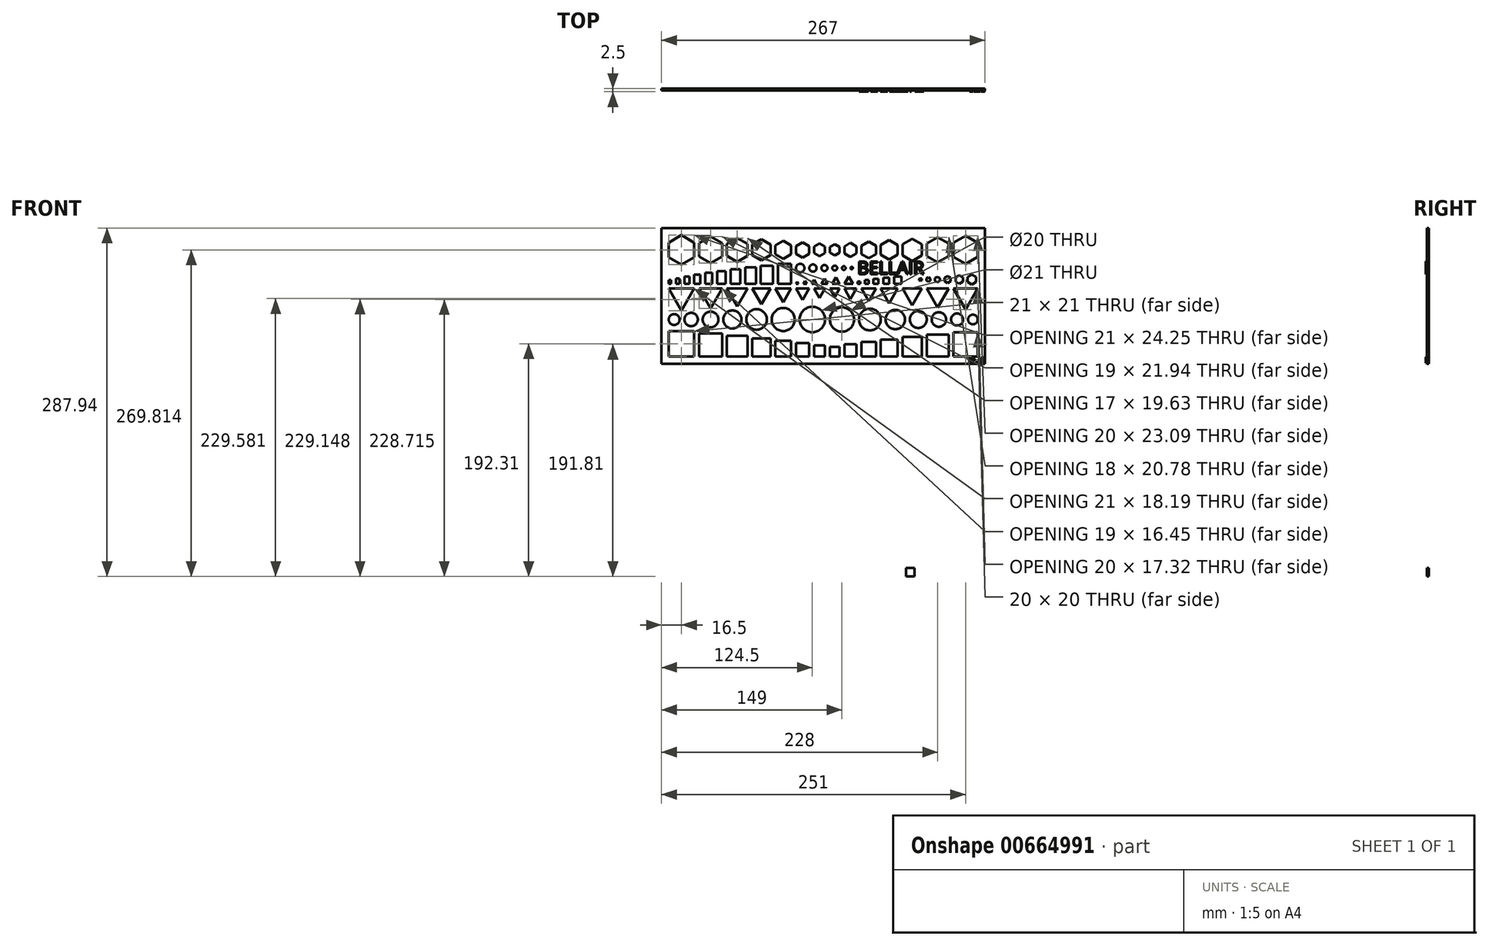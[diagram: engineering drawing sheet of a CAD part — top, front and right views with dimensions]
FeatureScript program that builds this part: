
annotation { "Feature Type Name" : "Feature", "Feature Type Description" : "" }
export const myFeature = defineFeature(function(context is Context, id is Id, definition is map)
    precondition{}
    {
        {
            var Q0;
            Q0=qCreatedBy(makeId("Front.planeOp"),FACE);
            var sketch = newSketch(context, id + "F0", { "sketchPlane" : qUnion([Q0])});
            skLineSegment(sketch, "E0.bottom", {"start": v(0, 0) * mm, "end": v(8, 0) * mm});
            skLineSegment(sketch, "E0.top", {"start": v(0, 8) * mm, "end": v(8, 8) * mm});
            skLineSegment(sketch, "E0.left", {"start": v(0, 0) * mm, "end": v(0, 8) * mm});
            skLineSegment(sketch, "E0.right", {"start": v(8, 0) * mm, "end": v(8, 8) * mm});
            skLineSegment(sketch, "E1.bottom", {"start": v(12, 0) * mm, "end": v(22, 0) * mm});
            skLineSegment(sketch, "E1.top", {"start": v(12, 10) * mm, "end": v(22, 10) * mm});
            skLineSegment(sketch, "E1.left", {"start": v(12, 0) * mm, "end": v(12, 10) * mm});
            skLineSegment(sketch, "E1.right", {"start": v(22, 0) * mm, "end": v(22, 10) * mm});
            skLineSegment(sketch, "E2.bottom", {"start": v(26, 0) * mm, "end": v(38, 0) * mm});
            skLineSegment(sketch, "E2.top", {"start": v(26, 12) * mm, "end": v(38, 12) * mm});
            skLineSegment(sketch, "E2.left", {"start": v(26, 0) * mm, "end": v(26, 12) * mm});
            skLineSegment(sketch, "E2.right", {"start": v(38, 0) * mm, "end": v(38, 12) * mm});
            skLineSegment(sketch, "E3.bottom", {"start": v(42, 0) * mm, "end": v(56, 0) * mm});
            skLineSegment(sketch, "E3.top", {"start": v(42, 14) * mm, "end": v(56, 14) * mm});
            skLineSegment(sketch, "E3.left", {"start": v(42, 0) * mm, "end": v(42, 14) * mm});
            skLineSegment(sketch, "E3.right", {"start": v(56, 0) * mm, "end": v(56, 14) * mm});
            skLineSegment(sketch, "E4.bottom", {"start": v(60, 0) * mm, "end": v(76, 0) * mm});
            skLineSegment(sketch, "E4.top", {"start": v(60, 16) * mm, "end": v(76, 16) * mm});
            skLineSegment(sketch, "E4.left", {"start": v(60, 0) * mm, "end": v(60, 16) * mm});
            skLineSegment(sketch, "E4.right", {"start": v(76, 0) * mm, "end": v(76, 16) * mm});
            skLineSegment(sketch, "E5.bottom", {"start": v(80, 0) * mm, "end": v(98, 0) * mm});
            skLineSegment(sketch, "E5.top", {"start": v(80, 18) * mm, "end": v(98, 18) * mm});
            skLineSegment(sketch, "E5.left", {"start": v(80, 0) * mm, "end": v(80, 18) * mm});
            skLineSegment(sketch, "E5.right", {"start": v(98, 0) * mm, "end": v(98, 18) * mm});
            skLineSegment(sketch, "E6.bottom", {"start": v(102, 0) * mm, "end": v(122, 0) * mm});
            skLineSegment(sketch, "E6.top", {"start": v(102, 20) * mm, "end": v(122, 20) * mm});
            skLineSegment(sketch, "E6.left", {"start": v(102, 0) * mm, "end": v(102, 20) * mm});
            skLineSegment(sketch, "E6.right", {"start": v(122, 0) * mm, "end": v(122, 20) * mm});
            skCircle(sketch, "E7", {"center": v(118, 30.5) * mm, "radius": 4 * mm});
            skCircle(sketch, "E8", {"center": v(105, 30.5) * mm, "radius": 5 * mm});
            skCircle(sketch, "E9", {"center": v(73, 30.5) * mm, "radius": 7 * mm});
            skCircle(sketch, "E10", {"center": v(90, 30.5) * mm, "radius": 6 * mm});
            skCircle(sketch, "E11", {"center": v(54, 30.5) * mm, "radius": 8 * mm});
            skCircle(sketch, "E12", {"center": v(33, 30.5) * mm, "radius": 9 * mm});
            skCircle(sketch, "E13", {"center": v(10, 30.5) * mm, "radius": 10 * mm});
            skLineSegment(sketch, "E14.bottom", {"start": v(-4, 0) * mm, "end": v(-13, 0) * mm});
            skLineSegment(sketch, "E14.top", {"start": v(-4, 9) * mm, "end": v(-13, 9) * mm});
            skLineSegment(sketch, "E14.left", {"start": v(-4, 0) * mm, "end": v(-4, 9) * mm});
            skLineSegment(sketch, "E14.right", {"start": v(-13, 0) * mm, "end": v(-13, 9) * mm});
            skLineSegment(sketch, "E15.bottom", {"start": v(-17, 0) * mm, "end": v(-28, 0) * mm});
            skLineSegment(sketch, "E15.top", {"start": v(-17, 11) * mm, "end": v(-28, 11) * mm});
            skLineSegment(sketch, "E15.left", {"start": v(-17, 0) * mm, "end": v(-17, 11) * mm});
            skLineSegment(sketch, "E15.right", {"start": v(-28, 0) * mm, "end": v(-28, 11) * mm});
            skLineSegment(sketch, "E16.bottom", {"start": v(-32, 0) * mm, "end": v(-45, 0) * mm});
            skLineSegment(sketch, "E16.top", {"start": v(-32, 13) * mm, "end": v(-45, 13) * mm});
            skLineSegment(sketch, "E16.left", {"start": v(-32, 0) * mm, "end": v(-32, 13) * mm});
            skLineSegment(sketch, "E16.right", {"start": v(-45, 0) * mm, "end": v(-45, 13) * mm});
            skLineSegment(sketch, "E17.bottom", {"start": v(-49, 0) * mm, "end": v(-64, 0) * mm});
            skLineSegment(sketch, "E17.top", {"start": v(-49, 15) * mm, "end": v(-64, 15) * mm});
            skLineSegment(sketch, "E17.left", {"start": v(-49, 0) * mm, "end": v(-49, 15) * mm});
            skLineSegment(sketch, "E17.right", {"start": v(-64, 0) * mm, "end": v(-64, 15) * mm});
            skLineSegment(sketch, "E18.bottom", {"start": v(-68, 0) * mm, "end": v(-85, 0) * mm});
            skLineSegment(sketch, "E18.top", {"start": v(-68, 17) * mm, "end": v(-85, 17) * mm});
            skLineSegment(sketch, "E18.left", {"start": v(-68, 0) * mm, "end": v(-68, 17) * mm});
            skLineSegment(sketch, "E18.right", {"start": v(-85, 0) * mm, "end": v(-85, 17) * mm});
            skLineSegment(sketch, "E19.bottom", {"start": v(-89, 0) * mm, "end": v(-108, 0) * mm});
            skLineSegment(sketch, "E19.top", {"start": v(-89, 19) * mm, "end": v(-108, 19) * mm});
            skLineSegment(sketch, "E19.left", {"start": v(-89, 0) * mm, "end": v(-89, 19) * mm});
            skLineSegment(sketch, "E19.right", {"start": v(-108, 0) * mm, "end": v(-108, 19) * mm});
            skLineSegment(sketch, "E20.bottom", {"start": v(-112, 0) * mm, "end": v(-133, 0) * mm});
            skLineSegment(sketch, "E20.top", {"start": v(-112, 21) * mm, "end": v(-133, 21) * mm});
            skLineSegment(sketch, "E20.left", {"start": v(-112, 0) * mm, "end": v(-112, 21) * mm});
            skLineSegment(sketch, "E20.right", {"start": v(-133, 0) * mm, "end": v(-133, 21) * mm});
            skCircle(sketch, "E21", {"center": v(-38.5, 30.5) * mm, "radius": 9.5 * mm});
            skCircle(sketch, "E22", {"center": v(-60.5, 30.5) * mm, "radius": 8.5 * mm});
            skCircle(sketch, "E23", {"center": v(-80.5, 30.5) * mm, "radius": 7.5 * mm});
            skCircle(sketch, "E24", {"center": v(-128.5, 30.5) * mm, "radius": 4.5 * mm});
            skCircle(sketch, "E25", {"center": v(-98.5, 30.5) * mm, "radius": 6.5 * mm});
            skCircle(sketch, "E26", {"center": v(-114.5, 30.5) * mm, "radius": 5.5 * mm});
            skCircle(sketch, "E27", {"center": v(-14.5, 30.5) * mm, "radius": 10.5 * mm});
            skCircle(sketch, "E28.cCircle", {"center": v(4, 53.69) * mm, "radius": 2.3 * mm, "construction": true});
            skLineSegment(sketch, "E28.0", {"start": v(0, 56) * mm, "end": v(8, 56) * mm});
            skLineSegment(sketch, "E28.1", {"start": v(8, 56) * mm, "end": v(4, 49.07) * mm});
            skLineSegment(sketch, "E28.2", {"start": v(4, 49.07) * mm, "end": v(0, 56) * mm});
            skPoint(sketch, "E28.0.midPoint", {"position": v(4, 56) * mm});
            skCircle(sketch, "E29.cCircle", {"center": v(17, 53.11) * mm, "radius": 2.89 * mm, "construction": true});
            skLineSegment(sketch, "E29.0", {"start": v(12, 56) * mm, "end": v(22, 56) * mm});
            skLineSegment(sketch, "E29.1", {"start": v(22, 56) * mm, "end": v(17, 47.34) * mm});
            skLineSegment(sketch, "E29.2", {"start": v(17, 47.34) * mm, "end": v(12, 56) * mm});
            skPoint(sketch, "E29.0.midPoint", {"position": v(17, 56) * mm});
            skCircle(sketch, "E30.cCircle", {"center": v(32, 52.53) * mm, "radius": 3.46 * mm, "construction": true});
            skLineSegment(sketch, "E30.0", {"start": v(26, 56) * mm, "end": v(38, 56) * mm});
            skLineSegment(sketch, "E30.1", {"start": v(38, 56) * mm, "end": v(32, 45.6) * mm});
            skLineSegment(sketch, "E30.2", {"start": v(32, 45.6) * mm, "end": v(26, 56) * mm});
            skPoint(sketch, "E30.0.midPoint", {"position": v(32, 56) * mm});
            skCircle(sketch, "E31.cCircle", {"center": v(49, 51.96) * mm, "radius": 4.04 * mm, "construction": true});
            skLineSegment(sketch, "E31.0", {"start": v(42, 56) * mm, "end": v(56, 56) * mm});
            skLineSegment(sketch, "E31.1", {"start": v(56, 56) * mm, "end": v(49, 43.87) * mm});
            skLineSegment(sketch, "E31.2", {"start": v(49, 43.87) * mm, "end": v(42, 56) * mm});
            skPoint(sketch, "E31.0.midPoint", {"position": v(49, 56) * mm});
            skCircle(sketch, "E32.cCircle", {"center": v(68, 51.38) * mm, "radius": 4.62 * mm, "construction": true});
            skLineSegment(sketch, "E32.0", {"start": v(60, 56) * mm, "end": v(76, 56) * mm});
            skLineSegment(sketch, "E32.1", {"start": v(76, 56) * mm, "end": v(68, 42.14) * mm});
            skLineSegment(sketch, "E32.2", {"start": v(68, 42.14) * mm, "end": v(60, 56) * mm});
            skPoint(sketch, "E32.0.midPoint", {"position": v(68, 56) * mm});
            skCircle(sketch, "E33.cCircle", {"center": v(89, 50.8) * mm, "radius": 5.2 * mm, "construction": true});
            skLineSegment(sketch, "E33.0", {"start": v(80, 56) * mm, "end": v(98, 56) * mm});
            skLineSegment(sketch, "E33.1", {"start": v(98, 56) * mm, "end": v(89, 40.4) * mm});
            skLineSegment(sketch, "E33.2", {"start": v(89, 40.4) * mm, "end": v(80, 56) * mm});
            skPoint(sketch, "E33.0.midPoint", {"position": v(89, 56) * mm});
            skCircle(sketch, "E34.cCircle", {"center": v(112, 50.22) * mm, "radius": 5.77 * mm, "construction": true});
            skLineSegment(sketch, "E34.0", {"start": v(102, 56) * mm, "end": v(122, 56) * mm});
            skLineSegment(sketch, "E34.1", {"start": v(122, 56) * mm, "end": v(112, 38.68) * mm});
            skLineSegment(sketch, "E34.2", {"start": v(112, 38.68) * mm, "end": v(102, 56) * mm});
            skPoint(sketch, "E34.0.midPoint", {"position": v(112, 56) * mm});
            skCircle(sketch, "E35.cCircle", {"center": v(-8.5, 53.4) * mm, "radius": 2.6 * mm, "construction": true});
            skLineSegment(sketch, "E35.0", {"start": v(-13, 56) * mm, "end": v(-4, 56) * mm});
            skLineSegment(sketch, "E35.1", {"start": v(-4, 56) * mm, "end": v(-8.5, 48.2) * mm});
            skLineSegment(sketch, "E35.2", {"start": v(-8.5, 48.2) * mm, "end": v(-13, 56) * mm});
            skPoint(sketch, "E35.0.midPoint", {"position": v(-8.5, 56) * mm});
            skCircle(sketch, "E36.cCircle", {"center": v(-22.5, 52.82) * mm, "radius": 3.18 * mm, "construction": true});
            skLineSegment(sketch, "E36.0", {"start": v(-28, 56) * mm, "end": v(-17, 56) * mm});
            skLineSegment(sketch, "E36.1", {"start": v(-17, 56) * mm, "end": v(-22.5, 46.47) * mm});
            skLineSegment(sketch, "E36.2", {"start": v(-22.5, 46.47) * mm, "end": v(-28, 56) * mm});
            skPoint(sketch, "E36.0.midPoint", {"position": v(-22.5, 56) * mm});
            skCircle(sketch, "E37.cCircle", {"center": v(-38.5, 52.25) * mm, "radius": 3.75 * mm, "construction": true});
            skLineSegment(sketch, "E37.0", {"start": v(-45, 56) * mm, "end": v(-32, 56) * mm});
            skLineSegment(sketch, "E37.1", {"start": v(-32, 56) * mm, "end": v(-38.5, 44.74) * mm});
            skLineSegment(sketch, "E37.2", {"start": v(-38.5, 44.74) * mm, "end": v(-45, 56) * mm});
            skPoint(sketch, "E37.0.midPoint", {"position": v(-38.5, 56) * mm});
            skCircle(sketch, "E38.cCircle", {"center": v(-56.5, 51.67) * mm, "radius": 4.33 * mm, "construction": true});
            skLineSegment(sketch, "E38.0", {"start": v(-64, 56) * mm, "end": v(-49, 56) * mm});
            skLineSegment(sketch, "E38.1", {"start": v(-49, 56) * mm, "end": v(-56.5, 43) * mm});
            skLineSegment(sketch, "E38.2", {"start": v(-56.5, 43) * mm, "end": v(-64, 56) * mm});
            skPoint(sketch, "E38.0.midPoint", {"position": v(-56.5, 56) * mm});
            skCircle(sketch, "E39.cCircle", {"center": v(-76.5, 51.1) * mm, "radius": 4.9 * mm, "construction": true});
            skLineSegment(sketch, "E39.0", {"start": v(-85, 56) * mm, "end": v(-68, 56) * mm});
            skLineSegment(sketch, "E39.1", {"start": v(-68, 56) * mm, "end": v(-76.5, 41.28) * mm});
            skLineSegment(sketch, "E39.2", {"start": v(-76.5, 41.28) * mm, "end": v(-85, 56) * mm});
            skPoint(sketch, "E39.0.midPoint", {"position": v(-76.5, 56) * mm});
            skCircle(sketch, "E40.cCircle", {"center": v(-98.5, 50.51) * mm, "radius": 5.48 * mm, "construction": true});
            skLineSegment(sketch, "E40.0", {"start": v(-108, 56) * mm, "end": v(-89, 56) * mm});
            skLineSegment(sketch, "E40.1", {"start": v(-89, 56) * mm, "end": v(-98.5, 39.54) * mm});
            skLineSegment(sketch, "E40.2", {"start": v(-98.5, 39.54) * mm, "end": v(-108, 56) * mm});
            skPoint(sketch, "E40.0.midPoint", {"position": v(-98.5, 56) * mm});
            skCircle(sketch, "E41.cCircle", {"center": v(-122.5, 49.94) * mm, "radius": 6.06 * mm, "construction": true});
            skLineSegment(sketch, "E41.0", {"start": v(-133, 56) * mm, "end": v(-112, 56) * mm});
            skLineSegment(sketch, "E41.1", {"start": v(-112, 56) * mm, "end": v(-122.5, 37.81) * mm});
            skLineSegment(sketch, "E41.2", {"start": v(-122.5, 37.81) * mm, "end": v(-133, 56) * mm});
            skPoint(sketch, "E41.0.midPoint", {"position": v(-122.5, 56) * mm});
            skLineSegment(sketch, "E42.bottom", {"start": v(-133, 60) * mm, "end": v(-131, 60) * mm});
            skLineSegment(sketch, "E42.top", {"start": v(-133, 63) * mm, "end": v(-131, 63) * mm});
            skLineSegment(sketch, "E42.left", {"start": v(-133, 60) * mm, "end": v(-133, 63) * mm});
            skLineSegment(sketch, "E42.right", {"start": v(-131, 60) * mm, "end": v(-131, 63) * mm});
            skLineSegment(sketch, "E43.bottom", {"start": v(-127, 60) * mm, "end": v(-124, 60) * mm});
            skLineSegment(sketch, "E43.top", {"start": v(-127, 64.5) * mm, "end": v(-124, 64.5) * mm});
            skLineSegment(sketch, "E43.left", {"start": v(-127, 60) * mm, "end": v(-127, 64.5) * mm});
            skLineSegment(sketch, "E43.right", {"start": v(-124, 60) * mm, "end": v(-124, 64.5) * mm});
            skLineSegment(sketch, "E44.bottom", {"start": v(-120, 60) * mm, "end": v(-116, 60) * mm});
            skLineSegment(sketch, "E44.top", {"start": v(-120, 66) * mm, "end": v(-116, 66) * mm});
            skLineSegment(sketch, "E44.left", {"start": v(-120, 60) * mm, "end": v(-120, 66) * mm});
            skLineSegment(sketch, "E44.right", {"start": v(-116, 60) * mm, "end": v(-116, 66) * mm});
            skLineSegment(sketch, "E45.bottom", {"start": v(-112, 60) * mm, "end": v(-107, 60) * mm});
            skLineSegment(sketch, "E45.top", {"start": v(-112, 67.5) * mm, "end": v(-107, 67.5) * mm});
            skLineSegment(sketch, "E45.left", {"start": v(-112, 60) * mm, "end": v(-112, 67.5) * mm});
            skLineSegment(sketch, "E45.right", {"start": v(-107, 60) * mm, "end": v(-107, 67.5) * mm});
            skLineSegment(sketch, "E46.bottom", {"start": v(-103, 60) * mm, "end": v(-97, 60) * mm});
            skLineSegment(sketch, "E46.top", {"start": v(-103, 69) * mm, "end": v(-97, 69) * mm});
            skLineSegment(sketch, "E46.left", {"start": v(-103, 60) * mm, "end": v(-103, 69) * mm});
            skLineSegment(sketch, "E46.right", {"start": v(-97, 60) * mm, "end": v(-97, 69) * mm});
            skLineSegment(sketch, "E47.bottom", {"start": v(-93, 60) * mm, "end": v(-86, 60) * mm});
            skLineSegment(sketch, "E47.top", {"start": v(-93, 70.5) * mm, "end": v(-86, 70.5) * mm});
            skLineSegment(sketch, "E47.left", {"start": v(-93, 60) * mm, "end": v(-93, 70.5) * mm});
            skLineSegment(sketch, "E47.right", {"start": v(-86, 60) * mm, "end": v(-86, 70.5) * mm});
            skLineSegment(sketch, "E48.bottom", {"start": v(-82, 60) * mm, "end": v(-74, 60) * mm});
            skLineSegment(sketch, "E48.top", {"start": v(-82, 72) * mm, "end": v(-74, 72) * mm});
            skLineSegment(sketch, "E48.left", {"start": v(-82, 60) * mm, "end": v(-82, 72) * mm});
            skLineSegment(sketch, "E48.right", {"start": v(-74, 60) * mm, "end": v(-74, 72) * mm});
            skLineSegment(sketch, "E49.bottom", {"start": v(-70, 60) * mm, "end": v(-61, 60) * mm});
            skLineSegment(sketch, "E49.top", {"start": v(-70, 73.5) * mm, "end": v(-61, 73.5) * mm});
            skLineSegment(sketch, "E49.left", {"start": v(-70, 60) * mm, "end": v(-70, 73.5) * mm});
            skLineSegment(sketch, "E49.right", {"start": v(-61, 60) * mm, "end": v(-61, 73.5) * mm});
            skLineSegment(sketch, "E50.bottom", {"start": v(-57, 60) * mm, "end": v(-47, 60) * mm});
            skLineSegment(sketch, "E50.top", {"start": v(-57, 75) * mm, "end": v(-47, 75) * mm});
            skLineSegment(sketch, "E50.left", {"start": v(-57, 60) * mm, "end": v(-57, 75) * mm});
            skLineSegment(sketch, "E50.right", {"start": v(-47, 60) * mm, "end": v(-47, 75) * mm});
            skLineSegment(sketch, "E51.bottom", {"start": v(-43, 60) * mm, "end": v(-32, 60) * mm});
            skLineSegment(sketch, "E51.top", {"start": v(-43, 76.5) * mm, "end": v(-32, 76.5) * mm});
            skLineSegment(sketch, "E51.left", {"start": v(-43, 60) * mm, "end": v(-43, 76.5) * mm});
            skLineSegment(sketch, "E51.right", {"start": v(-32, 60) * mm, "end": v(-32, 76.5) * mm});
            skCircle(sketch, "E52.cCircle", {"center": v(-27, 60.58) * mm, "radius": 0.58 * mm, "construction": true});
            skLineSegment(sketch, "E52.0", {"start": v(-26, 60) * mm, "end": v(-28, 60) * mm});
            skLineSegment(sketch, "E52.1", {"start": v(-28, 60) * mm, "end": v(-27, 61.73) * mm});
            skLineSegment(sketch, "E52.2", {"start": v(-27, 61.73) * mm, "end": v(-26, 60) * mm});
            skPoint(sketch, "E52.0.midPoint", {"position": v(-27, 60) * mm});
            skCircle(sketch, "E53.cCircle", {"center": v(-20.5, 60.86) * mm, "radius": 0.87 * mm, "construction": true});
            skPoint(sketch, "E53.cCircle.perimeterSnap0", {"position": v(-5.5, 60) * mm});
            skLineSegment(sketch, "E53.0", {"start": v(-19, 60) * mm, "end": v(-22, 60) * mm});
            skLineSegment(sketch, "E53.1", {"start": v(-22, 60) * mm, "end": v(-20.5, 62.6) * mm});
            skLineSegment(sketch, "E53.2", {"start": v(-20.5, 62.6) * mm, "end": v(-19, 60) * mm});
            skPoint(sketch, "E53.0.midPoint", {"position": v(-20.5, 60) * mm});
            skPoint(sketch, "E53.0.midPoint.positionSnap0", {"position": v(-5.5, 60) * mm});
            skCircle(sketch, "E54.cCircle", {"center": v(-13, 61.15) * mm, "radius": 1.15 * mm, "construction": true});
            skLineSegment(sketch, "E54.0", {"start": v(-11, 60) * mm, "end": v(-15, 60) * mm});
            skLineSegment(sketch, "E54.1", {"start": v(-15, 60) * mm, "end": v(-13, 63.46) * mm});
            skLineSegment(sketch, "E54.2", {"start": v(-13, 63.46) * mm, "end": v(-11, 60) * mm});
            skPoint(sketch, "E54.0.midPoint", {"position": v(-13, 60) * mm});
            skCircle(sketch, "E55.cCircle", {"center": v(-4.5, 61.44) * mm, "radius": 1.44 * mm, "construction": true});
            skLineSegment(sketch, "E55.0", {"start": v(-2, 60) * mm, "end": v(-7, 60) * mm});
            skLineSegment(sketch, "E55.1", {"start": v(-7, 60) * mm, "end": v(-4.5, 64.33) * mm});
            skLineSegment(sketch, "E55.2", {"start": v(-4.5, 64.33) * mm, "end": v(-2, 60) * mm});
            skPoint(sketch, "E55.0.midPoint", {"position": v(-4.5, 60) * mm});
            skCircle(sketch, "E56.cCircle", {"center": v(5, 61.73) * mm, "radius": 1.73 * mm, "construction": true});
            skLineSegment(sketch, "E56.0", {"start": v(8, 60) * mm, "end": v(2, 60) * mm});
            skLineSegment(sketch, "E56.1", {"start": v(2, 60) * mm, "end": v(5, 65.2) * mm});
            skLineSegment(sketch, "E56.2", {"start": v(5, 65.2) * mm, "end": v(8, 60) * mm});
            skPoint(sketch, "E56.0.midPoint", {"position": v(5, 60) * mm});
            skCircle(sketch, "E57.cCircle", {"center": v(15.5, 62.02) * mm, "radius": 2.02 * mm, "construction": true});
            skLineSegment(sketch, "E57.0", {"start": v(19, 60) * mm, "end": v(12, 60) * mm});
            skLineSegment(sketch, "E57.1", {"start": v(12, 60) * mm, "end": v(15.5, 66.06) * mm});
            skLineSegment(sketch, "E57.2", {"start": v(15.5, 66.06) * mm, "end": v(19, 60) * mm});
            skPoint(sketch, "E57.0.midPoint", {"position": v(15.5, 60) * mm});
            skLineSegment(sketch, "E58", {"start": v(-28, 60) * mm, "end": v(-28, 75.51) * mm});
            skCircle(sketch, "E59", {"center": v(-24.5, 73) * mm, "radius": 3.5 * mm});
            skCircle(sketch, "E60", {"center": v(-14, 73) * mm, "radius": 3 * mm});
            skCircle(sketch, "E61", {"center": v(-4.5, 73) * mm, "radius": 2.5 * mm});
            skCircle(sketch, "E62", {"center": v(4, 73) * mm, "radius": 2 * mm});
            skCircle(sketch, "E63", {"center": v(11.5, 73) * mm, "radius": 1.5 * mm});
            skCircle(sketch, "E64", {"center": v(18, 73) * mm, "radius": 1 * mm});
            skLineSegment(sketch, "E65.bottom", {"start": v(23, 60) * mm, "end": v(25, 60) * mm});
            skLineSegment(sketch, "E65.top", {"start": v(23, 62) * mm, "end": v(25, 62) * mm});
            skLineSegment(sketch, "E65.left", {"start": v(23, 60) * mm, "end": v(23, 62) * mm});
            skLineSegment(sketch, "E65.right", {"start": v(25, 60) * mm, "end": v(25, 62) * mm});
            skLineSegment(sketch, "E66.bottom", {"start": v(29, 60) * mm, "end": v(32, 60) * mm});
            skLineSegment(sketch, "E66.top", {"start": v(29, 63) * mm, "end": v(32, 63) * mm});
            skLineSegment(sketch, "E66.left", {"start": v(29, 60) * mm, "end": v(29, 63) * mm});
            skLineSegment(sketch, "E66.right", {"start": v(32, 60) * mm, "end": v(32, 63) * mm});
            skLineSegment(sketch, "E67.bottom", {"start": v(36, 60) * mm, "end": v(40, 60) * mm});
            skLineSegment(sketch, "E67.top", {"start": v(36, 64) * mm, "end": v(40, 64) * mm});
            skLineSegment(sketch, "E67.left", {"start": v(36, 60) * mm, "end": v(36, 64) * mm});
            skLineSegment(sketch, "E67.right", {"start": v(40, 60) * mm, "end": v(40, 64) * mm});
            skLineSegment(sketch, "E68.bottom", {"start": v(44, 60) * mm, "end": v(49, 60) * mm});
            skLineSegment(sketch, "E68.top", {"start": v(44, 65) * mm, "end": v(49, 65) * mm});
            skLineSegment(sketch, "E68.left", {"start": v(44, 60) * mm, "end": v(44, 65) * mm});
            skLineSegment(sketch, "E68.right", {"start": v(49, 60) * mm, "end": v(49, 65) * mm});
            skLineSegment(sketch, "E69.bottom", {"start": v(53, 60) * mm, "end": v(59, 60) * mm});
            skLineSegment(sketch, "E69.top", {"start": v(53, 66) * mm, "end": v(59, 66) * mm});
            skLineSegment(sketch, "E69.left", {"start": v(53, 60) * mm, "end": v(53, 66) * mm});
            skLineSegment(sketch, "E69.right", {"start": v(59, 60) * mm, "end": v(59, 66) * mm});
            skLineSegment(sketch, "E70.bottom", {"start": v(63, -181.81) * mm, "end": v(70, -181.81) * mm});
            skLineSegment(sketch, "E70.top", {"start": v(63, -174.81) * mm, "end": v(70, -174.81) * mm});
            skLineSegment(sketch, "E70.left", {"start": v(63, -181.81) * mm, "end": v(63, -174.81) * mm});
            skLineSegment(sketch, "E70.right", {"start": v(70, -181.81) * mm, "end": v(70, -174.81) * mm});
            skCircle(sketch, "E71.cCircle", {"center": v(74.74, 63.5) * mm, "radius": 1 * mm, "construction": true});
            skLineSegment(sketch, "E71.0", {"start": v(75.73, 64.08) * mm, "end": v(75.74, 62.92) * mm});
            skLineSegment(sketch, "E71.1", {"start": v(75.74, 62.92) * mm, "end": v(74.74, 62.34) * mm});
            skLineSegment(sketch, "E71.2", {"start": v(74.74, 62.34) * mm, "end": v(73.74, 62.92) * mm});
            skLineSegment(sketch, "E71.3", {"start": v(73.74, 62.92) * mm, "end": v(73.73, 64.07) * mm});
            skLineSegment(sketch, "E71.4", {"start": v(73.73, 64.07) * mm, "end": v(74.73, 64.65) * mm});
            skLineSegment(sketch, "E71.5", {"start": v(74.73, 64.65) * mm, "end": v(75.73, 64.08) * mm});
            skPoint(sketch, "E71.0.midPoint", {"position": v(75.74, 63.5) * mm});
            skCircle(sketch, "E72.cCircle", {"center": v(81.24, 63.5) * mm, "radius": 1.5 * mm, "construction": true});
            skLineSegment(sketch, "E72.0", {"start": v(82.73, 64.37) * mm, "end": v(82.74, 62.63) * mm});
            skLineSegment(sketch, "E72.1", {"start": v(82.74, 62.63) * mm, "end": v(81.24, 61.77) * mm});
            skLineSegment(sketch, "E72.2", {"start": v(81.24, 61.77) * mm, "end": v(79.74, 62.63) * mm});
            skLineSegment(sketch, "E72.3", {"start": v(79.74, 62.63) * mm, "end": v(79.73, 64.36) * mm});
            skLineSegment(sketch, "E72.4", {"start": v(79.73, 64.36) * mm, "end": v(81.23, 65.23) * mm});
            skLineSegment(sketch, "E72.5", {"start": v(81.23, 65.23) * mm, "end": v(82.73, 64.37) * mm});
            skPoint(sketch, "E72.0.midPoint", {"position": v(82.74, 63.5) * mm});
            skCircle(sketch, "E73.cCircle", {"center": v(88.74, 63.5) * mm, "radius": 2 * mm, "construction": true});
            skLineSegment(sketch, "E73.0", {"start": v(86.74, 62.34) * mm, "end": v(86.73, 64.65) * mm});
            skLineSegment(sketch, "E73.1", {"start": v(86.73, 64.65) * mm, "end": v(88.73, 65.8) * mm});
            skLineSegment(sketch, "E73.2", {"start": v(88.73, 65.8) * mm, "end": v(90.73, 64.66) * mm});
            skLineSegment(sketch, "E73.3", {"start": v(90.73, 64.66) * mm, "end": v(90.74, 62.35) * mm});
            skLineSegment(sketch, "E73.4", {"start": v(90.74, 62.35) * mm, "end": v(88.74, 61.19) * mm});
            skLineSegment(sketch, "E73.5", {"start": v(88.74, 61.19) * mm, "end": v(86.74, 62.34) * mm});
            skPoint(sketch, "E73.0.midPoint", {"position": v(86.74, 63.5) * mm});
            skCircle(sketch, "E74.cCircle", {"center": v(97.24, 63.5) * mm, "radius": 2.5 * mm, "construction": true});
            skLineSegment(sketch, "E74.0", {"start": v(99.73, 64.94) * mm, "end": v(99.74, 62.06) * mm});
            skLineSegment(sketch, "E74.1", {"start": v(99.74, 62.06) * mm, "end": v(97.24, 60.61) * mm});
            skLineSegment(sketch, "E74.2", {"start": v(97.24, 60.61) * mm, "end": v(94.74, 62.05) * mm});
            skLineSegment(sketch, "E74.3", {"start": v(94.74, 62.05) * mm, "end": v(94.73, 64.94) * mm});
            skLineSegment(sketch, "E74.4", {"start": v(94.73, 64.94) * mm, "end": v(97.23, 66.38) * mm});
            skLineSegment(sketch, "E74.5", {"start": v(97.23, 66.38) * mm, "end": v(99.73, 64.94) * mm});
            skPoint(sketch, "E74.0.midPoint", {"position": v(99.74, 63.5) * mm});
            skCircle(sketch, "E75.cCircle", {"center": v(106.74, 63.5) * mm, "radius": 3 * mm, "construction": true});
            skLineSegment(sketch, "E75.0", {"start": v(109.73, 65.23) * mm, "end": v(109.74, 61.77) * mm});
            skLineSegment(sketch, "E75.1", {"start": v(109.74, 61.77) * mm, "end": v(106.74, 60.03) * mm});
            skLineSegment(sketch, "E75.2", {"start": v(106.74, 60.03) * mm, "end": v(103.74, 61.76) * mm});
            skLineSegment(sketch, "E75.3", {"start": v(103.74, 61.76) * mm, "end": v(103.73, 65.23) * mm});
            skLineSegment(sketch, "E75.4", {"start": v(103.73, 65.23) * mm, "end": v(106.73, 66.96) * mm});
            skLineSegment(sketch, "E75.5", {"start": v(106.73, 66.96) * mm, "end": v(109.73, 65.23) * mm});
            skPoint(sketch, "E75.0.midPoint", {"position": v(109.74, 63.5) * mm});
            skCircle(sketch, "E76.cCircle", {"center": v(117.24, 63.5) * mm, "radius": 3.5 * mm, "construction": true});
            skLineSegment(sketch, "E76.0", {"start": v(120.73, 65.52) * mm, "end": v(120.74, 61.48) * mm});
            skLineSegment(sketch, "E76.1", {"start": v(120.74, 61.48) * mm, "end": v(117.24, 59.46) * mm});
            skLineSegment(sketch, "E76.2", {"start": v(117.24, 59.46) * mm, "end": v(113.74, 61.47) * mm});
            skLineSegment(sketch, "E76.3", {"start": v(113.74, 61.47) * mm, "end": v(113.73, 65.51) * mm});
            skLineSegment(sketch, "E76.4", {"start": v(113.73, 65.51) * mm, "end": v(117.23, 67.54) * mm});
            skLineSegment(sketch, "E76.5", {"start": v(117.23, 67.54) * mm, "end": v(120.73, 65.52) * mm});
            skPoint(sketch, "E76.0.midPoint", {"position": v(120.74, 63.5) * mm});
            skCircle(sketch, "E77.cCircle", {"center": v(4, 88) * mm, "radius": 4 * mm, "construction": true});
            skLineSegment(sketch, "E77.0", {"start": v(0, 85.7) * mm, "end": v(0, 90.31) * mm});
            skLineSegment(sketch, "E77.1", {"start": v(0, 90.31) * mm, "end": v(4, 92.62) * mm});
            skLineSegment(sketch, "E77.2", {"start": v(4, 92.62) * mm, "end": v(8, 90.31) * mm});
            skLineSegment(sketch, "E77.3", {"start": v(8, 90.31) * mm, "end": v(8, 85.7) * mm});
            skLineSegment(sketch, "E77.4", {"start": v(8, 85.7) * mm, "end": v(4, 83.38) * mm});
            skLineSegment(sketch, "E77.5", {"start": v(4, 83.38) * mm, "end": v(0, 85.7) * mm});
            skPoint(sketch, "E77.0.midPoint", {"position": v(0, 88) * mm});
            skCircle(sketch, "E78.cCircle", {"center": v(17, 88) * mm, "radius": 5 * mm, "construction": true});
            skLineSegment(sketch, "E78.0", {"start": v(22, 90.9) * mm, "end": v(22, 85.12) * mm});
            skLineSegment(sketch, "E78.1", {"start": v(22, 85.12) * mm, "end": v(17, 82.23) * mm});
            skLineSegment(sketch, "E78.2", {"start": v(17, 82.23) * mm, "end": v(12, 85.12) * mm});
            skLineSegment(sketch, "E78.3", {"start": v(12, 85.12) * mm, "end": v(12, 90.9) * mm});
            skLineSegment(sketch, "E78.4", {"start": v(12, 90.9) * mm, "end": v(17, 93.78) * mm});
            skLineSegment(sketch, "E78.5", {"start": v(17, 93.78) * mm, "end": v(22, 90.9) * mm});
            skPoint(sketch, "E78.0.midPoint", {"position": v(22, 88) * mm});
            skCircle(sketch, "E79.cCircle", {"center": v(32, 88) * mm, "radius": 6 * mm, "construction": true});
            skLineSegment(sketch, "E79.0", {"start": v(26, 84.54) * mm, "end": v(26, 91.47) * mm});
            skLineSegment(sketch, "E79.1", {"start": v(26, 91.47) * mm, "end": v(32, 94.93) * mm});
            skLineSegment(sketch, "E79.2", {"start": v(32, 94.93) * mm, "end": v(38, 91.47) * mm});
            skLineSegment(sketch, "E79.3", {"start": v(38, 91.47) * mm, "end": v(38, 84.54) * mm});
            skLineSegment(sketch, "E79.4", {"start": v(38, 84.54) * mm, "end": v(32, 81.08) * mm});
            skLineSegment(sketch, "E79.5", {"start": v(32, 81.08) * mm, "end": v(26, 84.54) * mm});
            skPoint(sketch, "E79.0.midPoint", {"position": v(26, 88) * mm});
            skCircle(sketch, "E80.cCircle", {"center": v(49, 88) * mm, "radius": 7 * mm, "construction": true});
            skLineSegment(sketch, "E80.0", {"start": v(42, 83.96) * mm, "end": v(42, 92.05) * mm});
            skLineSegment(sketch, "E80.1", {"start": v(42, 92.05) * mm, "end": v(49, 96.09) * mm});
            skLineSegment(sketch, "E80.2", {"start": v(49, 96.09) * mm, "end": v(56, 92.05) * mm});
            skLineSegment(sketch, "E80.3", {"start": v(56, 92.05) * mm, "end": v(56, 83.96) * mm});
            skLineSegment(sketch, "E80.4", {"start": v(56, 83.96) * mm, "end": v(49, 79.92) * mm});
            skLineSegment(sketch, "E80.5", {"start": v(49, 79.92) * mm, "end": v(42, 83.96) * mm});
            skPoint(sketch, "E80.0.midPoint", {"position": v(42, 88) * mm});
            skCircle(sketch, "E81.cCircle", {"center": v(68, 88) * mm, "radius": 8 * mm, "construction": true});
            skLineSegment(sketch, "E81.0", {"start": v(60, 83.38) * mm, "end": v(60, 92.62) * mm});
            skLineSegment(sketch, "E81.1", {"start": v(60, 92.62) * mm, "end": v(68, 97.24) * mm});
            skLineSegment(sketch, "E81.2", {"start": v(68, 97.24) * mm, "end": v(76, 92.62) * mm});
            skLineSegment(sketch, "E81.3", {"start": v(76, 92.62) * mm, "end": v(76, 83.38) * mm});
            skLineSegment(sketch, "E81.4", {"start": v(76, 83.38) * mm, "end": v(68, 78.77) * mm});
            skLineSegment(sketch, "E81.5", {"start": v(68, 78.77) * mm, "end": v(60, 83.38) * mm});
            skPoint(sketch, "E81.0.midPoint", {"position": v(60, 88) * mm});
            skCircle(sketch, "E82.cCircle", {"center": v(89, 88) * mm, "radius": 9 * mm, "construction": true});
            skLineSegment(sketch, "E82.0", {"start": v(80, 82.8) * mm, "end": v(80, 93.2) * mm});
            skLineSegment(sketch, "E82.1", {"start": v(80, 93.2) * mm, "end": v(89, 98.4) * mm});
            skLineSegment(sketch, "E82.2", {"start": v(89, 98.4) * mm, "end": v(98, 93.2) * mm});
            skLineSegment(sketch, "E82.3", {"start": v(98, 93.2) * mm, "end": v(98, 82.8) * mm});
            skLineSegment(sketch, "E82.4", {"start": v(98, 82.8) * mm, "end": v(89, 77.61) * mm});
            skLineSegment(sketch, "E82.5", {"start": v(89, 77.61) * mm, "end": v(80, 82.8) * mm});
            skPoint(sketch, "E82.0.midPoint", {"position": v(80, 88) * mm});
            skCircle(sketch, "E83.cCircle", {"center": v(112, 88) * mm, "radius": 10 * mm, "construction": true});
            skLineSegment(sketch, "E83.0", {"start": v(102, 82.23) * mm, "end": v(102, 93.78) * mm});
            skLineSegment(sketch, "E83.1", {"start": v(102, 93.78) * mm, "end": v(112, 99.55) * mm});
            skLineSegment(sketch, "E83.2", {"start": v(112, 99.55) * mm, "end": v(122, 93.78) * mm});
            skLineSegment(sketch, "E83.3", {"start": v(122, 93.78) * mm, "end": v(122, 82.23) * mm});
            skLineSegment(sketch, "E83.4", {"start": v(122, 82.23) * mm, "end": v(112, 76.46) * mm});
            skLineSegment(sketch, "E83.5", {"start": v(112, 76.46) * mm, "end": v(102, 82.23) * mm});
            skPoint(sketch, "E83.0.midPoint", {"position": v(102, 88) * mm});
            skCircle(sketch, "E84.cCircle", {"center": v(-8.5, 88) * mm, "radius": 4.5 * mm, "construction": true});
            skLineSegment(sketch, "E84.0", {"start": v(-13, 85.4) * mm, "end": v(-13, 90.6) * mm});
            skLineSegment(sketch, "E84.1", {"start": v(-13, 90.6) * mm, "end": v(-8.5, 93.2) * mm});
            skLineSegment(sketch, "E84.2", {"start": v(-8.5, 93.2) * mm, "end": v(-4, 90.6) * mm});
            skLineSegment(sketch, "E84.3", {"start": v(-4, 90.6) * mm, "end": v(-4, 85.4) * mm});
            skLineSegment(sketch, "E84.4", {"start": v(-4, 85.4) * mm, "end": v(-8.5, 82.8) * mm});
            skLineSegment(sketch, "E84.5", {"start": v(-8.5, 82.8) * mm, "end": v(-13, 85.4) * mm});
            skPoint(sketch, "E84.0.midPoint", {"position": v(-13, 88) * mm});
            skCircle(sketch, "E85.cCircle", {"center": v(-22.5, 88) * mm, "radius": 5.5 * mm, "construction": true});
            skLineSegment(sketch, "E85.0", {"start": v(-28, 84.83) * mm, "end": v(-28, 91.18) * mm});
            skLineSegment(sketch, "E85.1", {"start": v(-28, 91.18) * mm, "end": v(-22.5, 94.35) * mm});
            skLineSegment(sketch, "E85.2", {"start": v(-22.5, 94.35) * mm, "end": v(-17, 91.18) * mm});
            skLineSegment(sketch, "E85.3", {"start": v(-17, 91.18) * mm, "end": v(-17, 84.83) * mm});
            skLineSegment(sketch, "E85.4", {"start": v(-17, 84.83) * mm, "end": v(-22.5, 81.65) * mm});
            skLineSegment(sketch, "E85.5", {"start": v(-22.5, 81.65) * mm, "end": v(-28, 84.83) * mm});
            skPoint(sketch, "E85.0.midPoint", {"position": v(-28, 88) * mm});
            skCircle(sketch, "E86.cCircle", {"center": v(-38.5, 88) * mm, "radius": 6.5 * mm, "construction": true});
            skLineSegment(sketch, "E86.0", {"start": v(-32, 91.76) * mm, "end": v(-32, 84.25) * mm});
            skLineSegment(sketch, "E86.1", {"start": v(-32, 84.25) * mm, "end": v(-38.5, 80.5) * mm});
            skLineSegment(sketch, "E86.2", {"start": v(-38.5, 80.5) * mm, "end": v(-45, 84.25) * mm});
            skLineSegment(sketch, "E86.3", {"start": v(-45, 84.25) * mm, "end": v(-45, 91.76) * mm});
            skLineSegment(sketch, "E86.4", {"start": v(-45, 91.76) * mm, "end": v(-38.5, 95.5) * mm});
            skLineSegment(sketch, "E86.5", {"start": v(-38.5, 95.5) * mm, "end": v(-32, 91.76) * mm});
            skPoint(sketch, "E86.0.midPoint", {"position": v(-32, 88) * mm});
            skCircle(sketch, "E87.cCircle", {"center": v(-56.5, 88) * mm, "radius": 7.5 * mm, "construction": true});
            skLineSegment(sketch, "E87.0", {"start": v(-49, 92.33) * mm, "end": v(-49, 83.67) * mm});
            skLineSegment(sketch, "E87.1", {"start": v(-49, 83.67) * mm, "end": v(-56.5, 79.34) * mm});
            skLineSegment(sketch, "E87.2", {"start": v(-56.5, 79.34) * mm, "end": v(-64, 83.67) * mm});
            skLineSegment(sketch, "E87.3", {"start": v(-64, 83.67) * mm, "end": v(-64, 92.33) * mm});
            skLineSegment(sketch, "E87.4", {"start": v(-64, 92.33) * mm, "end": v(-56.5, 96.66) * mm});
            skLineSegment(sketch, "E87.5", {"start": v(-56.5, 96.66) * mm, "end": v(-49, 92.33) * mm});
            skPoint(sketch, "E87.0.midPoint", {"position": v(-49, 88) * mm});
            skCircle(sketch, "E88.cCircle", {"center": v(-76.5, 88) * mm, "radius": 8.5 * mm, "construction": true});
            skLineSegment(sketch, "E88.0", {"start": v(-85, 83.1) * mm, "end": v(-85, 92.91) * mm});
            skLineSegment(sketch, "E88.1", {"start": v(-85, 92.91) * mm, "end": v(-76.5, 97.82) * mm});
            skLineSegment(sketch, "E88.2", {"start": v(-76.5, 97.82) * mm, "end": v(-68, 92.91) * mm});
            skLineSegment(sketch, "E88.3", {"start": v(-68, 92.91) * mm, "end": v(-68, 83.1) * mm});
            skLineSegment(sketch, "E88.4", {"start": v(-68, 83.1) * mm, "end": v(-76.5, 78.19) * mm});
            skLineSegment(sketch, "E88.5", {"start": v(-76.5, 78.19) * mm, "end": v(-85, 83.1) * mm});
            skPoint(sketch, "E88.0.midPoint", {"position": v(-85, 88) * mm});
            skCircle(sketch, "E89.cCircle", {"center": v(-98.5, 88) * mm, "radius": 9.5 * mm, "construction": true});
            skLineSegment(sketch, "E89.0", {"start": v(-108, 82.52) * mm, "end": v(-108, 93.49) * mm});
            skLineSegment(sketch, "E89.1", {"start": v(-108, 93.49) * mm, "end": v(-98.5, 98.97) * mm});
            skLineSegment(sketch, "E89.2", {"start": v(-98.5, 98.97) * mm, "end": v(-89, 93.49) * mm});
            skLineSegment(sketch, "E89.3", {"start": v(-89, 93.49) * mm, "end": v(-89, 82.52) * mm});
            skLineSegment(sketch, "E89.4", {"start": v(-89, 82.52) * mm, "end": v(-98.5, 77.03) * mm});
            skLineSegment(sketch, "E89.5", {"start": v(-98.5, 77.03) * mm, "end": v(-108, 82.52) * mm});
            skPoint(sketch, "E89.0.midPoint", {"position": v(-108, 88) * mm});
            skCircle(sketch, "E90.cCircle", {"center": v(-122.5, 88) * mm, "radius": 10.5 * mm, "construction": true});
            skLineSegment(sketch, "E90.0", {"start": v(-112, 94.07) * mm, "end": v(-112, 81.94) * mm});
            skLineSegment(sketch, "E90.1", {"start": v(-112, 81.94) * mm, "end": v(-122.5, 75.88) * mm});
            skLineSegment(sketch, "E90.2", {"start": v(-122.5, 75.88) * mm, "end": v(-133, 81.94) * mm});
            skLineSegment(sketch, "E90.3", {"start": v(-133, 81.94) * mm, "end": v(-133, 94.07) * mm});
            skLineSegment(sketch, "E90.4", {"start": v(-133, 94.07) * mm, "end": v(-122.5, 100.13) * mm});
            skLineSegment(sketch, "E90.5", {"start": v(-122.5, 100.13) * mm, "end": v(-112, 94.07) * mm});
            skPoint(sketch, "E90.0.midPoint", {"position": v(-112, 88) * mm});
            skLineSegment(sketch, "E91.bottom", {"start": v(-139, 106.13) * mm, "end": v(128, 106.13) * mm});
            skLineSegment(sketch, "E91.top", {"start": v(-139, -6) * mm, "end": v(128, -6) * mm});
            skLineSegment(sketch, "E91.left", {"start": v(-139, 106.13) * mm, "end": v(-139, -6) * mm});
            skLineSegment(sketch, "E91.right", {"start": v(128, 106.13) * mm, "end": v(128, -6) * mm});
            skSolve(sketch);
        }
        {
            var Q0;
            Q0=qSketchRegion(id+"F0",true);
            extrude(context, id + "F1", {"entities" : qUnion([Q0]), "depth" : 1.5 * mm, "offsetDistance" : 25 * mm});
        }
        {
            var Q0;
            Q0=makeQuery(id+"F1.opExtrude","CAP_FACE",FACE,{"disambiguationData":[OSD([sQuery(id+"F0.wireOp",EDGE,"E0.bottom"),sQuery(id+"F0.wireOp",EDGE,"E0.top"),sQuery(id+"F0.wireOp",EDGE,"E0.left"),sQuery(id+"F0.wireOp",EDGE,"E0.right"),sQuery(id+"F0.wireOp",EDGE,"E1.bottom"),sQuery(id+"F0.wireOp",EDGE,"E1.top"),sQuery(id+"F0.wireOp",EDGE,"E1.left"),sQuery(id+"F0.wireOp",EDGE,"E1.right"),sQuery(id+"F0.wireOp",EDGE,"E2.bottom"),sQuery(id+"F0.wireOp",EDGE,"E2.top"),sQuery(id+"F0.wireOp",EDGE,"E2.left"),sQuery(id+"F0.wireOp",EDGE,"E2.right"),sQuery(id+"F0.wireOp",EDGE,"E3.bottom"),sQuery(id+"F0.wireOp",EDGE,"E3.top"),sQuery(id+"F0.wireOp",EDGE,"E3.left"),sQuery(id+"F0.wireOp",EDGE,"E3.right"),sQuery(id+"F0.wireOp",EDGE,"E4.bottom"),sQuery(id+"F0.wireOp",EDGE,"E4.top"),sQuery(id+"F0.wireOp",EDGE,"E4.left"),sQuery(id+"F0.wireOp",EDGE,"E4.right"),sQuery(id+"F0.wireOp",EDGE,"E5.bottom"),sQuery(id+"F0.wireOp",EDGE,"E5.top"),sQuery(id+"F0.wireOp",EDGE,"E5.left"),sQuery(id+"F0.wireOp",EDGE,"E5.right"),sQuery(id+"F0.wireOp",EDGE,"E6.bottom"),sQuery(id+"F0.wireOp",EDGE,"E6.top"),sQuery(id+"F0.wireOp",EDGE,"E6.left"),sQuery(id+"F0.wireOp",EDGE,"E6.right"),sQuery(id+"F0.wireOp",EDGE,"E7"),sQuery(id+"F0.wireOp",EDGE,"E8"),sQuery(id+"F0.wireOp",EDGE,"E9"),sQuery(id+"F0.wireOp",EDGE,"E10"),sQuery(id+"F0.wireOp",EDGE,"E11"),sQuery(id+"F0.wireOp",EDGE,"E12"),sQuery(id+"F0.wireOp",EDGE,"E13"),sQuery(id+"F0.wireOp",EDGE,"E14.bottom"),sQuery(id+"F0.wireOp",EDGE,"E14.top"),sQuery(id+"F0.wireOp",EDGE,"E14.left"),sQuery(id+"F0.wireOp",EDGE,"E14.right"),sQuery(id+"F0.wireOp",EDGE,"E15.bottom"),sQuery(id+"F0.wireOp",EDGE,"E15.top"),sQuery(id+"F0.wireOp",EDGE,"E15.left"),sQuery(id+"F0.wireOp",EDGE,"E15.right"),sQuery(id+"F0.wireOp",EDGE,"E16.bottom"),sQuery(id+"F0.wireOp",EDGE,"E16.top"),sQuery(id+"F0.wireOp",EDGE,"E16.left"),sQuery(id+"F0.wireOp",EDGE,"E16.right"),sQuery(id+"F0.wireOp",EDGE,"E17.bottom"),sQuery(id+"F0.wireOp",EDGE,"E17.top"),sQuery(id+"F0.wireOp",EDGE,"E17.left"),sQuery(id+"F0.wireOp",EDGE,"E17.right"),sQuery(id+"F0.wireOp",EDGE,"E18.bottom"),sQuery(id+"F0.wireOp",EDGE,"E18.top"),sQuery(id+"F0.wireOp",EDGE,"E18.left"),sQuery(id+"F0.wireOp",EDGE,"E18.right"),sQuery(id+"F0.wireOp",EDGE,"E19.bottom"),sQuery(id+"F0.wireOp",EDGE,"E19.top"),sQuery(id+"F0.wireOp",EDGE,"E19.left"),sQuery(id+"F0.wireOp",EDGE,"E19.right"),sQuery(id+"F0.wireOp",EDGE,"E20.bottom"),sQuery(id+"F0.wireOp",EDGE,"E20.top"),sQuery(id+"F0.wireOp",EDGE,"E20.left"),sQuery(id+"F0.wireOp",EDGE,"E20.right"),sQuery(id+"F0.wireOp",EDGE,"E21"),sQuery(id+"F0.wireOp",EDGE,"E22"),sQuery(id+"F0.wireOp",EDGE,"E23"),sQuery(id+"F0.wireOp",EDGE,"E24"),sQuery(id+"F0.wireOp",EDGE,"E25"),sQuery(id+"F0.wireOp",EDGE,"E26"),sQuery(id+"F0.wireOp",EDGE,"E27"),sQuery(id+"F0.wireOp",EDGE,"E28.0"),sQuery(id+"F0.wireOp",EDGE,"E28.1"),sQuery(id+"F0.wireOp",EDGE,"E28.2"),sQuery(id+"F0.wireOp",EDGE,"E29.0"),sQuery(id+"F0.wireOp",EDGE,"E29.1"),sQuery(id+"F0.wireOp",EDGE,"E29.2"),sQuery(id+"F0.wireOp",EDGE,"E30.0"),sQuery(id+"F0.wireOp",EDGE,"E30.1"),sQuery(id+"F0.wireOp",EDGE,"E30.2"),sQuery(id+"F0.wireOp",EDGE,"E31.0"),sQuery(id+"F0.wireOp",EDGE,"E31.1"),sQuery(id+"F0.wireOp",EDGE,"E31.2"),sQuery(id+"F0.wireOp",EDGE,"E32.0"),sQuery(id+"F0.wireOp",EDGE,"E32.1"),sQuery(id+"F0.wireOp",EDGE,"E32.2"),sQuery(id+"F0.wireOp",EDGE,"E33.0"),sQuery(id+"F0.wireOp",EDGE,"E33.1"),sQuery(id+"F0.wireOp",EDGE,"E33.2"),sQuery(id+"F0.wireOp",EDGE,"E34.0"),sQuery(id+"F0.wireOp",EDGE,"E34.1"),sQuery(id+"F0.wireOp",EDGE,"E34.2"),sQuery(id+"F0.wireOp",EDGE,"E35.0"),sQuery(id+"F0.wireOp",EDGE,"E35.1"),sQuery(id+"F0.wireOp",EDGE,"E35.2"),sQuery(id+"F0.wireOp",EDGE,"E36.0"),sQuery(id+"F0.wireOp",EDGE,"E36.1"),sQuery(id+"F0.wireOp",EDGE,"E36.2"),sQuery(id+"F0.wireOp",EDGE,"E37.0"),sQuery(id+"F0.wireOp",EDGE,"E37.1"),sQuery(id+"F0.wireOp",EDGE,"E37.2"),sQuery(id+"F0.wireOp",EDGE,"E38.0"),sQuery(id+"F0.wireOp",EDGE,"E38.1"),sQuery(id+"F0.wireOp",EDGE,"E38.2"),sQuery(id+"F0.wireOp",EDGE,"E39.0"),sQuery(id+"F0.wireOp",EDGE,"E39.1"),sQuery(id+"F0.wireOp",EDGE,"E39.2"),sQuery(id+"F0.wireOp",EDGE,"E40.0"),sQuery(id+"F0.wireOp",EDGE,"E40.1"),sQuery(id+"F0.wireOp",EDGE,"E40.2"),sQuery(id+"F0.wireOp",EDGE,"E41.0"),sQuery(id+"F0.wireOp",EDGE,"E41.1"),sQuery(id+"F0.wireOp",EDGE,"E41.2"),sQuery(id+"F0.wireOp",EDGE,"E42.bottom"),sQuery(id+"F0.wireOp",EDGE,"E42.top"),sQuery(id+"F0.wireOp",EDGE,"E42.left"),sQuery(id+"F0.wireOp",EDGE,"E42.right"),sQuery(id+"F0.wireOp",EDGE,"E43.bottom"),sQuery(id+"F0.wireOp",EDGE,"E43.top"),sQuery(id+"F0.wireOp",EDGE,"E43.left"),sQuery(id+"F0.wireOp",EDGE,"E43.right"),sQuery(id+"F0.wireOp",EDGE,"E44.bottom"),sQuery(id+"F0.wireOp",EDGE,"E44.top"),sQuery(id+"F0.wireOp",EDGE,"E44.left"),sQuery(id+"F0.wireOp",EDGE,"E44.right"),sQuery(id+"F0.wireOp",EDGE,"E45.bottom"),sQuery(id+"F0.wireOp",EDGE,"E45.top"),sQuery(id+"F0.wireOp",EDGE,"E45.left"),sQuery(id+"F0.wireOp",EDGE,"E45.right"),sQuery(id+"F0.wireOp",EDGE,"E46.bottom"),sQuery(id+"F0.wireOp",EDGE,"E46.top"),sQuery(id+"F0.wireOp",EDGE,"E46.left"),sQuery(id+"F0.wireOp",EDGE,"E46.right"),sQuery(id+"F0.wireOp",EDGE,"E47.bottom"),sQuery(id+"F0.wireOp",EDGE,"E47.top"),sQuery(id+"F0.wireOp",EDGE,"E47.left"),sQuery(id+"F0.wireOp",EDGE,"E47.right"),sQuery(id+"F0.wireOp",EDGE,"E48.bottom"),sQuery(id+"F0.wireOp",EDGE,"E48.top"),sQuery(id+"F0.wireOp",EDGE,"E48.left"),sQuery(id+"F0.wireOp",EDGE,"E48.right"),sQuery(id+"F0.wireOp",EDGE,"E49.bottom"),sQuery(id+"F0.wireOp",EDGE,"E49.top"),sQuery(id+"F0.wireOp",EDGE,"E49.left"),sQuery(id+"F0.wireOp",EDGE,"E49.right"),sQuery(id+"F0.wireOp",EDGE,"E50.bottom"),sQuery(id+"F0.wireOp",EDGE,"E50.top"),sQuery(id+"F0.wireOp",EDGE,"E50.left"),sQuery(id+"F0.wireOp",EDGE,"E50.right"),sQuery(id+"F0.wireOp",EDGE,"E51.bottom"),sQuery(id+"F0.wireOp",EDGE,"E51.top"),sQuery(id+"F0.wireOp",EDGE,"E51.left"),sQuery(id+"F0.wireOp",EDGE,"E51.right"),sQuery(id+"F0.wireOp",EDGE,"E52.0"),sQuery(id+"F0.wireOp",EDGE,"E52.1"),sQuery(id+"F0.wireOp",EDGE,"E52.2"),sQuery(id+"F0.wireOp",EDGE,"E53.0"),sQuery(id+"F0.wireOp",EDGE,"E53.1"),sQuery(id+"F0.wireOp",EDGE,"E53.2"),sQuery(id+"F0.wireOp",EDGE,"E54.0"),sQuery(id+"F0.wireOp",EDGE,"E54.1"),sQuery(id+"F0.wireOp",EDGE,"E54.2"),sQuery(id+"F0.wireOp",EDGE,"E55.0"),sQuery(id+"F0.wireOp",EDGE,"E55.1"),sQuery(id+"F0.wireOp",EDGE,"E55.2"),sQuery(id+"F0.wireOp",EDGE,"E56.0"),sQuery(id+"F0.wireOp",EDGE,"E56.1"),sQuery(id+"F0.wireOp",EDGE,"E56.2"),sQuery(id+"F0.wireOp",EDGE,"E57.0"),sQuery(id+"F0.wireOp",EDGE,"E57.1"),sQuery(id+"F0.wireOp",EDGE,"E57.2"),sQuery(id+"F0.wireOp",EDGE,"E59"),sQuery(id+"F0.wireOp",EDGE,"E60"),sQuery(id+"F0.wireOp",EDGE,"E61"),sQuery(id+"F0.wireOp",EDGE,"E62"),sQuery(id+"F0.wireOp",EDGE,"E63"),sQuery(id+"F0.wireOp",EDGE,"E64"),sQuery(id+"F0.wireOp",EDGE,"E65.bottom"),sQuery(id+"F0.wireOp",EDGE,"E65.top"),sQuery(id+"F0.wireOp",EDGE,"E65.left"),sQuery(id+"F0.wireOp",EDGE,"E65.right"),sQuery(id+"F0.wireOp",EDGE,"E66.bottom"),sQuery(id+"F0.wireOp",EDGE,"E66.top"),sQuery(id+"F0.wireOp",EDGE,"E66.left"),sQuery(id+"F0.wireOp",EDGE,"E66.right"),sQuery(id+"F0.wireOp",EDGE,"E67.bottom"),sQuery(id+"F0.wireOp",EDGE,"E67.top"),sQuery(id+"F0.wireOp",EDGE,"E67.left"),sQuery(id+"F0.wireOp",EDGE,"E67.right"),sQuery(id+"F0.wireOp",EDGE,"E68.bottom"),sQuery(id+"F0.wireOp",EDGE,"E68.top"),sQuery(id+"F0.wireOp",EDGE,"E68.left"),sQuery(id+"F0.wireOp",EDGE,"E68.right"),sQuery(id+"F0.wireOp",EDGE,"E69.bottom"),sQuery(id+"F0.wireOp",EDGE,"E69.top"),sQuery(id+"F0.wireOp",EDGE,"E69.left"),sQuery(id+"F0.wireOp",EDGE,"E69.right"),sQuery(id+"F0.wireOp",EDGE,"E70.bottom"),sQuery(id+"F0.wireOp",EDGE,"E70.top"),sQuery(id+"F0.wireOp",EDGE,"E70.left"),sQuery(id+"F0.wireOp",EDGE,"E70.right"),sQuery(id+"F0.wireOp",EDGE,"E71.0"),sQuery(id+"F0.wireOp",EDGE,"E71.1"),sQuery(id+"F0.wireOp",EDGE,"E71.2"),sQuery(id+"F0.wireOp",EDGE,"E71.3"),sQuery(id+"F0.wireOp",EDGE,"E71.4"),sQuery(id+"F0.wireOp",EDGE,"E71.5"),sQuery(id+"F0.wireOp",EDGE,"E72.0"),sQuery(id+"F0.wireOp",EDGE,"E72.1"),sQuery(id+"F0.wireOp",EDGE,"E72.2"),sQuery(id+"F0.wireOp",EDGE,"E72.3"),sQuery(id+"F0.wireOp",EDGE,"E72.4"),sQuery(id+"F0.wireOp",EDGE,"E72.5"),sQuery(id+"F0.wireOp",EDGE,"E73.0"),sQuery(id+"F0.wireOp",EDGE,"E73.1"),sQuery(id+"F0.wireOp",EDGE,"E73.2"),sQuery(id+"F0.wireOp",EDGE,"E73.3"),sQuery(id+"F0.wireOp",EDGE,"E73.4"),sQuery(id+"F0.wireOp",EDGE,"E73.5"),sQuery(id+"F0.wireOp",EDGE,"E74.0"),sQuery(id+"F0.wireOp",EDGE,"E74.1"),sQuery(id+"F0.wireOp",EDGE,"E74.2"),sQuery(id+"F0.wireOp",EDGE,"E74.3"),sQuery(id+"F0.wireOp",EDGE,"E74.4"),sQuery(id+"F0.wireOp",EDGE,"E74.5"),sQuery(id+"F0.wireOp",EDGE,"E75.0"),sQuery(id+"F0.wireOp",EDGE,"E75.1"),sQuery(id+"F0.wireOp",EDGE,"E75.2"),sQuery(id+"F0.wireOp",EDGE,"E75.3"),sQuery(id+"F0.wireOp",EDGE,"E75.4"),sQuery(id+"F0.wireOp",EDGE,"E75.5"),sQuery(id+"F0.wireOp",EDGE,"E76.0"),sQuery(id+"F0.wireOp",EDGE,"E76.1"),sQuery(id+"F0.wireOp",EDGE,"E76.2"),sQuery(id+"F0.wireOp",EDGE,"E76.3"),sQuery(id+"F0.wireOp",EDGE,"E76.4"),sQuery(id+"F0.wireOp",EDGE,"E76.5"),sQuery(id+"F0.wireOp",EDGE,"E77.0"),sQuery(id+"F0.wireOp",EDGE,"E77.1"),sQuery(id+"F0.wireOp",EDGE,"E77.2"),sQuery(id+"F0.wireOp",EDGE,"E77.3"),sQuery(id+"F0.wireOp",EDGE,"E77.4"),sQuery(id+"F0.wireOp",EDGE,"E77.5"),sQuery(id+"F0.wireOp",EDGE,"E78.0"),sQuery(id+"F0.wireOp",EDGE,"E78.1"),sQuery(id+"F0.wireOp",EDGE,"E78.2"),sQuery(id+"F0.wireOp",EDGE,"E78.3"),sQuery(id+"F0.wireOp",EDGE,"E78.4"),sQuery(id+"F0.wireOp",EDGE,"E78.5"),sQuery(id+"F0.wireOp",EDGE,"E79.0"),sQuery(id+"F0.wireOp",EDGE,"E79.1"),sQuery(id+"F0.wireOp",EDGE,"E79.2"),sQuery(id+"F0.wireOp",EDGE,"E79.3"),sQuery(id+"F0.wireOp",EDGE,"E79.4"),sQuery(id+"F0.wireOp",EDGE,"E79.5"),sQuery(id+"F0.wireOp",EDGE,"E80.0"),sQuery(id+"F0.wireOp",EDGE,"E80.1"),sQuery(id+"F0.wireOp",EDGE,"E80.2"),sQuery(id+"F0.wireOp",EDGE,"E80.3"),sQuery(id+"F0.wireOp",EDGE,"E80.4"),sQuery(id+"F0.wireOp",EDGE,"E80.5"),sQuery(id+"F0.wireOp",EDGE,"E81.0"),sQuery(id+"F0.wireOp",EDGE,"E81.1"),sQuery(id+"F0.wireOp",EDGE,"E81.2"),sQuery(id+"F0.wireOp",EDGE,"E81.3"),sQuery(id+"F0.wireOp",EDGE,"E81.4"),sQuery(id+"F0.wireOp",EDGE,"E81.5"),sQuery(id+"F0.wireOp",EDGE,"E82.0"),sQuery(id+"F0.wireOp",EDGE,"E82.1"),sQuery(id+"F0.wireOp",EDGE,"E82.2"),sQuery(id+"F0.wireOp",EDGE,"E82.3"),sQuery(id+"F0.wireOp",EDGE,"E82.4"),sQuery(id+"F0.wireOp",EDGE,"E82.5"),sQuery(id+"F0.wireOp",EDGE,"E83.0"),sQuery(id+"F0.wireOp",EDGE,"E83.1"),sQuery(id+"F0.wireOp",EDGE,"E83.2"),sQuery(id+"F0.wireOp",EDGE,"E83.3"),sQuery(id+"F0.wireOp",EDGE,"E83.4"),sQuery(id+"F0.wireOp",EDGE,"E83.5"),sQuery(id+"F0.wireOp",EDGE,"E84.0"),sQuery(id+"F0.wireOp",EDGE,"E84.1"),sQuery(id+"F0.wireOp",EDGE,"E84.2"),sQuery(id+"F0.wireOp",EDGE,"E84.3"),sQuery(id+"F0.wireOp",EDGE,"E84.4"),sQuery(id+"F0.wireOp",EDGE,"E84.5"),sQuery(id+"F0.wireOp",EDGE,"E85.0"),sQuery(id+"F0.wireOp",EDGE,"E85.1"),sQuery(id+"F0.wireOp",EDGE,"E85.2"),sQuery(id+"F0.wireOp",EDGE,"E85.3"),sQuery(id+"F0.wireOp",EDGE,"E85.4"),sQuery(id+"F0.wireOp",EDGE,"E85.5"),sQuery(id+"F0.wireOp",EDGE,"E86.0"),sQuery(id+"F0.wireOp",EDGE,"E86.1"),sQuery(id+"F0.wireOp",EDGE,"E86.2"),sQuery(id+"F0.wireOp",EDGE,"E86.3"),sQuery(id+"F0.wireOp",EDGE,"E86.4"),sQuery(id+"F0.wireOp",EDGE,"E86.5"),sQuery(id+"F0.wireOp",EDGE,"E87.0"),sQuery(id+"F0.wireOp",EDGE,"E87.1"),sQuery(id+"F0.wireOp",EDGE,"E87.2"),sQuery(id+"F0.wireOp",EDGE,"E87.3"),sQuery(id+"F0.wireOp",EDGE,"E87.4"),sQuery(id+"F0.wireOp",EDGE,"E87.5"),sQuery(id+"F0.wireOp",EDGE,"E88.0"),sQuery(id+"F0.wireOp",EDGE,"E88.1"),sQuery(id+"F0.wireOp",EDGE,"E88.2"),sQuery(id+"F0.wireOp",EDGE,"E88.3"),sQuery(id+"F0.wireOp",EDGE,"E88.4"),sQuery(id+"F0.wireOp",EDGE,"E88.5"),sQuery(id+"F0.wireOp",EDGE,"E89.0"),sQuery(id+"F0.wireOp",EDGE,"E89.1"),sQuery(id+"F0.wireOp",EDGE,"E89.2"),sQuery(id+"F0.wireOp",EDGE,"E89.3"),sQuery(id+"F0.wireOp",EDGE,"E89.4"),sQuery(id+"F0.wireOp",EDGE,"E89.5"),sQuery(id+"F0.wireOp",EDGE,"E90.0"),sQuery(id+"F0.wireOp",EDGE,"E90.1"),sQuery(id+"F0.wireOp",EDGE,"E90.2"),sQuery(id+"F0.wireOp",EDGE,"E90.3"),sQuery(id+"F0.wireOp",EDGE,"E90.4"),sQuery(id+"F0.wireOp",EDGE,"E90.5"),sQuery(id+"F0.wireOp",EDGE,"E91.bottom"),sQuery(id+"F0.wireOp",EDGE,"E91.top"),sQuery(id+"F0.wireOp",EDGE,"E91.left"),sQuery(id+"F0.wireOp",EDGE,"E91.right")])],"isStart":false});
            var sketch = newSketch(context, id + "F2", { "sketchPlane" : qUnion([Q0])});
            skText(sketch, "E92", { "text": "BELLAIR", "fontName": "OpenSans-Regular.ttf"});
            const initialGuessF2  = {"E92": [0.0227, 0.06792, 1, 0, 0.0105]};
            skSetInitialGuess(sketch, initialGuessF2);
            skSolve(sketch);
        }
        {
            var Q0;
            Q0 = qSketchRegion(id + "F2", true);
            extrude(context, id + "F3", {"entities" : qUnion([Q0]), "operationType" : NewBodyOperationType.ADD, "depth" : 1 * mm, "offsetDistance" : 25 * mm});
        }
        {
            var Q0;
            {var subQ0=sQuery(id+"F0.wireOp",EDGE,"E69.right");var subQ1=sQuery(id+"F0.wireOp",EDGE,"E69.left");var subQ2=sQuery(id+"F0.wireOp",EDGE,"E69.top");var subQ3=sQuery(id+"F0.wireOp",EDGE,"E69.bottom");var subQ4=sQuery(id+"F0.wireOp",EDGE,"E68.right");var subQ5=sQuery(id+"F0.wireOp",EDGE,"E68.left");var subQ6=sQuery(id+"F0.wireOp",EDGE,"E68.top");var subQ7=sQuery(id+"F0.wireOp",EDGE,"E68.bottom");var subQ8=sQuery(id+"F0.wireOp",EDGE,"E67.right");var subQ9=sQuery(id+"F0.wireOp",EDGE,"E67.left");var subQ10=sQuery(id+"F0.wireOp",EDGE,"E67.top");var subQ11=sQuery(id+"F0.wireOp",EDGE,"E67.bottom");var subQ12=sQuery(id+"F0.wireOp",EDGE,"E66.right");var subQ13=sQuery(id+"F0.wireOp",EDGE,"E66.left");var subQ14=sQuery(id+"F0.wireOp",EDGE,"E66.top");var subQ15=sQuery(id+"F0.wireOp",EDGE,"E66.bottom");var subQ16=sQuery(id+"F0.wireOp",EDGE,"E65.right");var subQ17=sQuery(id+"F0.wireOp",EDGE,"E65.left");var subQ18=sQuery(id+"F0.wireOp",EDGE,"E65.top");var subQ19=sQuery(id+"F0.wireOp",EDGE,"E65.bottom");var subQ20=sQuery(id+"F0.wireOp",EDGE,"E64");var subQ21=sQuery(id+"F0.wireOp",EDGE,"E63");var subQ22=sQuery(id+"F0.wireOp",EDGE,"E62");var subQ23=sQuery(id+"F0.wireOp",EDGE,"E61");var subQ24=sQuery(id+"F0.wireOp",EDGE,"E60");var subQ25=sQuery(id+"F0.wireOp",EDGE,"E59");var subQ26=sQuery(id+"F0.wireOp",EDGE,"E57.2");var subQ27=sQuery(id+"F0.wireOp",EDGE,"E57.1");var subQ28=sQuery(id+"F0.wireOp",EDGE,"E57.0");var subQ29=sQuery(id+"F0.wireOp",EDGE,"E56.2");var subQ30=sQuery(id+"F0.wireOp",EDGE,"E56.1");var subQ31=sQuery(id+"F0.wireOp",EDGE,"E56.0");var subQ32=sQuery(id+"F0.wireOp",EDGE,"E55.2");var subQ33=sQuery(id+"F0.wireOp",EDGE,"E55.1");var subQ34=sQuery(id+"F0.wireOp",EDGE,"E55.0");var subQ35=sQuery(id+"F0.wireOp",EDGE,"E54.2");var subQ36=sQuery(id+"F0.wireOp",EDGE,"E54.1");var subQ37=sQuery(id+"F0.wireOp",EDGE,"E54.0");var subQ38=sQuery(id+"F0.wireOp",EDGE,"E53.2");var subQ39=sQuery(id+"F0.wireOp",EDGE,"E53.1");var subQ40=sQuery(id+"F0.wireOp",EDGE,"E53.0");var subQ41=sQuery(id+"F0.wireOp",EDGE,"E52.2");var subQ42=sQuery(id+"F0.wireOp",EDGE,"E52.1");var subQ43=sQuery(id+"F0.wireOp",EDGE,"E52.0");var subQ44=sQuery(id+"F0.wireOp",EDGE,"E51.right");var subQ45=sQuery(id+"F0.wireOp",EDGE,"E51.left");var subQ46=sQuery(id+"F0.wireOp",EDGE,"E51.top");var subQ47=sQuery(id+"F0.wireOp",EDGE,"E51.bottom");var subQ48=sQuery(id+"F0.wireOp",EDGE,"E50.right");var subQ49=sQuery(id+"F0.wireOp",EDGE,"E50.left");var subQ50=sQuery(id+"F0.wireOp",EDGE,"E50.top");var subQ51=sQuery(id+"F0.wireOp",EDGE,"E50.bottom");var subQ52=sQuery(id+"F0.wireOp",EDGE,"E49.right");var subQ53=sQuery(id+"F0.wireOp",EDGE,"E49.left");var subQ54=sQuery(id+"F0.wireOp",EDGE,"E49.top");var subQ55=sQuery(id+"F0.wireOp",EDGE,"E49.bottom");var subQ56=sQuery(id+"F0.wireOp",EDGE,"E48.right");var subQ57=sQuery(id+"F0.wireOp",EDGE,"E48.left");var subQ58=sQuery(id+"F0.wireOp",EDGE,"E48.top");var subQ59=sQuery(id+"F0.wireOp",EDGE,"E48.bottom");var subQ60=sQuery(id+"F0.wireOp",EDGE,"E47.right");var subQ61=sQuery(id+"F0.wireOp",EDGE,"E47.left");var subQ62=sQuery(id+"F0.wireOp",EDGE,"E47.top");var subQ63=sQuery(id+"F0.wireOp",EDGE,"E47.bottom");var subQ64=sQuery(id+"F0.wireOp",EDGE,"E46.right");var subQ65=sQuery(id+"F0.wireOp",EDGE,"E46.left");var subQ66=sQuery(id+"F0.wireOp",EDGE,"E46.top");var subQ67=sQuery(id+"F0.wireOp",EDGE,"E46.bottom");var subQ68=sQuery(id+"F0.wireOp",EDGE,"E45.right");var subQ69=sQuery(id+"F0.wireOp",EDGE,"E45.left");var subQ70=sQuery(id+"F0.wireOp",EDGE,"E45.top");var subQ71=sQuery(id+"F0.wireOp",EDGE,"E45.bottom");var subQ72=sQuery(id+"F0.wireOp",EDGE,"E44.right");var subQ73=sQuery(id+"F0.wireOp",EDGE,"E44.left");var subQ74=sQuery(id+"F0.wireOp",EDGE,"E44.top");var subQ75=sQuery(id+"F0.wireOp",EDGE,"E44.bottom");var subQ76=sQuery(id+"F0.wireOp",EDGE,"E43.right");var subQ77=sQuery(id+"F0.wireOp",EDGE,"E43.left");var subQ78=sQuery(id+"F0.wireOp",EDGE,"E43.top");var subQ79=sQuery(id+"F0.wireOp",EDGE,"E43.bottom");var subQ80=sQuery(id+"F0.wireOp",EDGE,"E42.right");var subQ81=sQuery(id+"F0.wireOp",EDGE,"E42.left");var subQ82=sQuery(id+"F0.wireOp",EDGE,"E42.top");var subQ83=sQuery(id+"F0.wireOp",EDGE,"E42.bottom");var subQ84=sQuery(id+"F0.wireOp",EDGE,"E41.2");var subQ85=sQuery(id+"F0.wireOp",EDGE,"E41.1");var subQ86=sQuery(id+"F0.wireOp",EDGE,"E41.0");var subQ87=sQuery(id+"F0.wireOp",EDGE,"E40.2");var subQ88=sQuery(id+"F0.wireOp",EDGE,"E40.1");var subQ89=sQuery(id+"F0.wireOp",EDGE,"E40.0");var subQ90=sQuery(id+"F0.wireOp",EDGE,"E39.2");var subQ91=sQuery(id+"F0.wireOp",EDGE,"E39.1");var subQ92=sQuery(id+"F0.wireOp",EDGE,"E39.0");var subQ93=sQuery(id+"F0.wireOp",EDGE,"E38.2");var subQ94=sQuery(id+"F0.wireOp",EDGE,"E38.1");var subQ95=sQuery(id+"F0.wireOp",EDGE,"E38.0");var subQ96=sQuery(id+"F0.wireOp",EDGE,"E37.2");var subQ97=sQuery(id+"F0.wireOp",EDGE,"E37.1");var subQ98=sQuery(id+"F0.wireOp",EDGE,"E37.0");var subQ99=sQuery(id+"F0.wireOp",EDGE,"E36.2");var subQ100=sQuery(id+"F0.wireOp",EDGE,"E16.top");var subQ101=sQuery(id+"F0.wireOp",EDGE,"E16.bottom");var subQ102=sQuery(id+"F0.wireOp",EDGE,"E15.right");var subQ103=sQuery(id+"F0.wireOp",EDGE,"E15.left");var subQ104=sQuery(id+"F0.wireOp",EDGE,"E15.top");var subQ105=sQuery(id+"F0.wireOp",EDGE,"E15.bottom");var subQ106=sQuery(id+"F0.wireOp",EDGE,"E14.right");var subQ107=sQuery(id+"F0.wireOp",EDGE,"E14.left");var subQ108=sQuery(id+"F0.wireOp",EDGE,"E14.top");var subQ109=sQuery(id+"F0.wireOp",EDGE,"E14.bottom");var subQ110=sQuery(id+"F0.wireOp",EDGE,"E13");var subQ111=sQuery(id+"F0.wireOp",EDGE,"E12");var subQ112=sQuery(id+"F0.wireOp",EDGE,"E11");var subQ113=sQuery(id+"F0.wireOp",EDGE,"E10");var subQ114=sQuery(id+"F0.wireOp",EDGE,"E9");var subQ115=sQuery(id+"F0.wireOp",EDGE,"E8");var subQ116=sQuery(id+"F0.wireOp",EDGE,"E7");var subQ117=sQuery(id+"F0.wireOp",EDGE,"E6.right");var subQ118=sQuery(id+"F0.wireOp",EDGE,"E6.left");var subQ119=sQuery(id+"F0.wireOp",EDGE,"E6.top");var subQ120=sQuery(id+"F0.wireOp",EDGE,"E6.bottom");var subQ121=sQuery(id+"F0.wireOp",EDGE,"E5.right");var subQ122=sQuery(id+"F0.wireOp",EDGE,"E5.left");var subQ123=sQuery(id+"F0.wireOp",EDGE,"E2.bottom");var subQ124=sQuery(id+"F0.wireOp",EDGE,"E1.right");var subQ125=sQuery(id+"F0.wireOp",EDGE,"E1.left");var subQ126=sQuery(id+"F0.wireOp",EDGE,"E1.top");var subQ127=sQuery(id+"F0.wireOp",EDGE,"E71.1");var subQ128=sQuery(id+"F0.wireOp",EDGE,"E1.bottom");var subQ129=sQuery(id+"F0.wireOp",EDGE,"E2.top");var subQ130=sQuery(id+"F0.wireOp",EDGE,"E16.left");var subQ131=sQuery(id+"F0.wireOp",EDGE,"E0.bottom");var subQ132=sQuery(id+"F0.wireOp",EDGE,"E36.1");var subQ133=sQuery(id+"F0.wireOp",EDGE,"E5.top");var subQ134=sQuery(id+"F0.wireOp",EDGE,"E71.0");var subQ135=sQuery(id+"F0.wireOp",EDGE,"E0.right");var subQ136=sQuery(id+"F0.wireOp",EDGE,"E0.top");var subQ137=sQuery(id+"F0.wireOp",EDGE,"E0.left");var subQ138=sQuery(id+"F0.wireOp",EDGE,"E2.left");var subQ139=sQuery(id+"F0.wireOp",EDGE,"E2.right");var subQ140=sQuery(id+"F0.wireOp",EDGE,"E3.bottom");var subQ141=sQuery(id+"F0.wireOp",EDGE,"E3.top");var subQ142=sQuery(id+"F0.wireOp",EDGE,"E3.left");var subQ143=sQuery(id+"F0.wireOp",EDGE,"E3.right");var subQ144=sQuery(id+"F0.wireOp",EDGE,"E4.bottom");var subQ145=sQuery(id+"F0.wireOp",EDGE,"E4.top");var subQ146=sQuery(id+"F0.wireOp",EDGE,"E4.left");var subQ147=sQuery(id+"F0.wireOp",EDGE,"E4.right");var subQ148=sQuery(id+"F0.wireOp",EDGE,"E5.bottom");var subQ149=sQuery(id+"F0.wireOp",EDGE,"E16.right");var subQ150=sQuery(id+"F0.wireOp",EDGE,"E17.bottom");var subQ151=sQuery(id+"F0.wireOp",EDGE,"E17.top");var subQ152=sQuery(id+"F0.wireOp",EDGE,"E17.left");var subQ153=sQuery(id+"F0.wireOp",EDGE,"E17.right");var subQ154=sQuery(id+"F0.wireOp",EDGE,"E18.bottom");var subQ155=sQuery(id+"F0.wireOp",EDGE,"E18.top");var subQ156=sQuery(id+"F0.wireOp",EDGE,"E18.left");var subQ157=sQuery(id+"F0.wireOp",EDGE,"E18.right");var subQ158=sQuery(id+"F0.wireOp",EDGE,"E19.bottom");var subQ159=sQuery(id+"F0.wireOp",EDGE,"E19.top");var subQ160=sQuery(id+"F0.wireOp",EDGE,"E19.left");var subQ161=sQuery(id+"F0.wireOp",EDGE,"E19.right");var subQ162=sQuery(id+"F0.wireOp",EDGE,"E20.bottom");var subQ163=sQuery(id+"F0.wireOp",EDGE,"E20.top");var subQ164=sQuery(id+"F0.wireOp",EDGE,"E20.left");var subQ165=sQuery(id+"F0.wireOp",EDGE,"E20.right");var subQ166=sQuery(id+"F0.wireOp",EDGE,"E21");var subQ167=sQuery(id+"F0.wireOp",EDGE,"E22");var subQ168=sQuery(id+"F0.wireOp",EDGE,"E23");var subQ169=sQuery(id+"F0.wireOp",EDGE,"E24");var subQ170=sQuery(id+"F0.wireOp",EDGE,"E25");var subQ171=sQuery(id+"F0.wireOp",EDGE,"E26");var subQ172=sQuery(id+"F0.wireOp",EDGE,"E27");var subQ173=sQuery(id+"F0.wireOp",EDGE,"E28.0");var subQ174=sQuery(id+"F0.wireOp",EDGE,"E28.1");var subQ175=sQuery(id+"F0.wireOp",EDGE,"E28.2");var subQ176=sQuery(id+"F0.wireOp",EDGE,"E29.0");var subQ177=sQuery(id+"F0.wireOp",EDGE,"E29.1");var subQ178=sQuery(id+"F0.wireOp",EDGE,"E29.2");var subQ179=sQuery(id+"F0.wireOp",EDGE,"E30.0");var subQ180=sQuery(id+"F0.wireOp",EDGE,"E30.1");var subQ181=sQuery(id+"F0.wireOp",EDGE,"E30.2");var subQ182=sQuery(id+"F0.wireOp",EDGE,"E31.0");var subQ183=sQuery(id+"F0.wireOp",EDGE,"E31.1");var subQ184=sQuery(id+"F0.wireOp",EDGE,"E31.2");var subQ185=sQuery(id+"F0.wireOp",EDGE,"E32.0");var subQ186=sQuery(id+"F0.wireOp",EDGE,"E32.1");var subQ187=sQuery(id+"F0.wireOp",EDGE,"E32.2");var subQ188=sQuery(id+"F0.wireOp",EDGE,"E33.0");var subQ189=sQuery(id+"F0.wireOp",EDGE,"E33.1");var subQ190=sQuery(id+"F0.wireOp",EDGE,"E33.2");var subQ191=sQuery(id+"F0.wireOp",EDGE,"E34.0");var subQ192=sQuery(id+"F0.wireOp",EDGE,"E34.1");var subQ193=sQuery(id+"F0.wireOp",EDGE,"E34.2");var subQ194=sQuery(id+"F0.wireOp",EDGE,"E35.0");var subQ195=sQuery(id+"F0.wireOp",EDGE,"E35.1");var subQ196=sQuery(id+"F0.wireOp",EDGE,"E35.2");var subQ197=sQuery(id+"F0.wireOp",EDGE,"E36.0");var subQ198=sQuery(id+"F0.wireOp",EDGE,"E71.2");var subQ199=sQuery(id+"F0.wireOp",EDGE,"E71.3");var subQ200=sQuery(id+"F0.wireOp",EDGE,"E71.4");var subQ201=sQuery(id+"F0.wireOp",EDGE,"E71.5");var subQ202=sQuery(id+"F0.wireOp",EDGE,"E72.0");var subQ203=sQuery(id+"F0.wireOp",EDGE,"E72.1");var subQ204=sQuery(id+"F0.wireOp",EDGE,"E72.2");var subQ205=sQuery(id+"F0.wireOp",EDGE,"E72.3");var subQ206=sQuery(id+"F0.wireOp",EDGE,"E72.4");var subQ207=sQuery(id+"F0.wireOp",EDGE,"E72.5");var subQ208=sQuery(id+"F0.wireOp",EDGE,"E73.0");var subQ209=sQuery(id+"F0.wireOp",EDGE,"E73.1");var subQ210=sQuery(id+"F0.wireOp",EDGE,"E73.2");var subQ211=sQuery(id+"F0.wireOp",EDGE,"E73.3");var subQ212=sQuery(id+"F0.wireOp",EDGE,"E73.4");var subQ213=sQuery(id+"F0.wireOp",EDGE,"E73.5");var subQ214=sQuery(id+"F0.wireOp",EDGE,"E74.0");var subQ215=sQuery(id+"F0.wireOp",EDGE,"E74.1");var subQ216=sQuery(id+"F0.wireOp",EDGE,"E74.2");var subQ217=sQuery(id+"F0.wireOp",EDGE,"E74.3");var subQ218=sQuery(id+"F0.wireOp",EDGE,"E74.4");var subQ219=sQuery(id+"F0.wireOp",EDGE,"E74.5");var subQ220=sQuery(id+"F0.wireOp",EDGE,"E75.0");var subQ221=sQuery(id+"F0.wireOp",EDGE,"E75.1");var subQ222=sQuery(id+"F0.wireOp",EDGE,"E75.2");var subQ223=sQuery(id+"F0.wireOp",EDGE,"E75.3");var subQ224=sQuery(id+"F0.wireOp",EDGE,"E75.4");var subQ225=sQuery(id+"F0.wireOp",EDGE,"E75.5");var subQ226=sQuery(id+"F0.wireOp",EDGE,"E76.0");var subQ227=sQuery(id+"F0.wireOp",EDGE,"E76.1");var subQ228=sQuery(id+"F0.wireOp",EDGE,"E76.2");var subQ229=sQuery(id+"F0.wireOp",EDGE,"E76.3");var subQ230=sQuery(id+"F0.wireOp",EDGE,"E76.4");var subQ231=sQuery(id+"F0.wireOp",EDGE,"E76.5");var subQ232=sQuery(id+"F0.wireOp",EDGE,"E77.0");var subQ233=sQuery(id+"F0.wireOp",EDGE,"E77.1");var subQ234=sQuery(id+"F0.wireOp",EDGE,"E77.2");var subQ235=sQuery(id+"F0.wireOp",EDGE,"E77.3");var subQ236=sQuery(id+"F0.wireOp",EDGE,"E77.4");var subQ237=sQuery(id+"F0.wireOp",EDGE,"E77.5");var subQ238=sQuery(id+"F0.wireOp",EDGE,"E78.0");var subQ239=sQuery(id+"F0.wireOp",EDGE,"E78.1");var subQ240=sQuery(id+"F0.wireOp",EDGE,"E78.2");var subQ241=sQuery(id+"F0.wireOp",EDGE,"E78.3");var subQ242=sQuery(id+"F0.wireOp",EDGE,"E78.4");var subQ243=sQuery(id+"F0.wireOp",EDGE,"E78.5");var subQ244=sQuery(id+"F0.wireOp",EDGE,"E79.0");var subQ245=sQuery(id+"F0.wireOp",EDGE,"E79.1");var subQ246=sQuery(id+"F0.wireOp",EDGE,"E79.2");var subQ247=sQuery(id+"F0.wireOp",EDGE,"E79.3");var subQ248=sQuery(id+"F0.wireOp",EDGE,"E79.4");var subQ249=sQuery(id+"F0.wireOp",EDGE,"E79.5");var subQ250=sQuery(id+"F0.wireOp",EDGE,"E80.0");var subQ251=sQuery(id+"F0.wireOp",EDGE,"E80.1");var subQ252=sQuery(id+"F0.wireOp",EDGE,"E80.2");var subQ253=sQuery(id+"F0.wireOp",EDGE,"E80.3");var subQ254=sQuery(id+"F0.wireOp",EDGE,"E80.4");var subQ255=sQuery(id+"F0.wireOp",EDGE,"E80.5");var subQ256=sQuery(id+"F0.wireOp",EDGE,"E81.0");var subQ257=sQuery(id+"F0.wireOp",EDGE,"E81.1");var subQ258=sQuery(id+"F0.wireOp",EDGE,"E81.2");var subQ259=sQuery(id+"F0.wireOp",EDGE,"E81.3");var subQ260=sQuery(id+"F0.wireOp",EDGE,"E81.4");var subQ261=sQuery(id+"F0.wireOp",EDGE,"E81.5");var subQ262=sQuery(id+"F0.wireOp",EDGE,"E82.0");var subQ263=sQuery(id+"F0.wireOp",EDGE,"E82.1");var subQ264=sQuery(id+"F0.wireOp",EDGE,"E82.2");var subQ265=sQuery(id+"F0.wireOp",EDGE,"E82.3");var subQ266=sQuery(id+"F0.wireOp",EDGE,"E82.4");var subQ267=sQuery(id+"F0.wireOp",EDGE,"E82.5");var subQ268=sQuery(id+"F0.wireOp",EDGE,"E83.0");var subQ269=sQuery(id+"F0.wireOp",EDGE,"E83.1");var subQ270=sQuery(id+"F0.wireOp",EDGE,"E83.2");var subQ271=sQuery(id+"F0.wireOp",EDGE,"E83.3");var subQ272=sQuery(id+"F0.wireOp",EDGE,"E83.4");var subQ273=sQuery(id+"F0.wireOp",EDGE,"E83.5");var subQ274=sQuery(id+"F0.wireOp",EDGE,"E84.0");var subQ275=sQuery(id+"F0.wireOp",EDGE,"E84.1");var subQ276=sQuery(id+"F0.wireOp",EDGE,"E84.2");var subQ277=sQuery(id+"F0.wireOp",EDGE,"E84.3");var subQ278=sQuery(id+"F0.wireOp",EDGE,"E84.4");var subQ279=sQuery(id+"F0.wireOp",EDGE,"E84.5");var subQ280=sQuery(id+"F0.wireOp",EDGE,"E85.0");var subQ281=sQuery(id+"F0.wireOp",EDGE,"E85.1");var subQ282=sQuery(id+"F0.wireOp",EDGE,"E85.2");var subQ283=sQuery(id+"F0.wireOp",EDGE,"E85.3");var subQ284=sQuery(id+"F0.wireOp",EDGE,"E85.4");var subQ285=sQuery(id+"F0.wireOp",EDGE,"E85.5");var subQ286=sQuery(id+"F0.wireOp",EDGE,"E86.0");var subQ287=sQuery(id+"F0.wireOp",EDGE,"E86.1");var subQ288=sQuery(id+"F0.wireOp",EDGE,"E86.2");var subQ289=sQuery(id+"F0.wireOp",EDGE,"E86.3");var subQ290=sQuery(id+"F0.wireOp",EDGE,"E86.4");var subQ291=sQuery(id+"F0.wireOp",EDGE,"E86.5");var subQ292=sQuery(id+"F0.wireOp",EDGE,"E87.0");var subQ293=sQuery(id+"F0.wireOp",EDGE,"E87.1");var subQ294=sQuery(id+"F0.wireOp",EDGE,"E87.2");var subQ295=sQuery(id+"F0.wireOp",EDGE,"E87.3");var subQ296=sQuery(id+"F0.wireOp",EDGE,"E87.4");var subQ297=sQuery(id+"F0.wireOp",EDGE,"E87.5");var subQ298=sQuery(id+"F0.wireOp",EDGE,"E88.0");var subQ299=sQuery(id+"F0.wireOp",EDGE,"E88.1");var subQ300=sQuery(id+"F0.wireOp",EDGE,"E88.2");var subQ301=sQuery(id+"F0.wireOp",EDGE,"E88.3");var subQ302=sQuery(id+"F0.wireOp",EDGE,"E88.4");var subQ303=sQuery(id+"F0.wireOp",EDGE,"E88.5");var subQ304=sQuery(id+"F0.wireOp",EDGE,"E89.0");var subQ305=sQuery(id+"F0.wireOp",EDGE,"E89.1");var subQ306=sQuery(id+"F0.wireOp",EDGE,"E89.2");var subQ307=sQuery(id+"F0.wireOp",EDGE,"E89.3");var subQ308=sQuery(id+"F0.wireOp",EDGE,"E89.4");var subQ309=sQuery(id+"F0.wireOp",EDGE,"E89.5");var subQ310=sQuery(id+"F0.wireOp",EDGE,"E90.0");var subQ311=sQuery(id+"F0.wireOp",EDGE,"E90.1");var subQ312=sQuery(id+"F0.wireOp",EDGE,"E90.2");var subQ313=sQuery(id+"F0.wireOp",EDGE,"E90.3");var subQ314=sQuery(id+"F0.wireOp",EDGE,"E90.4");var subQ315=sQuery(id+"F0.wireOp",EDGE,"E90.5");var subQ316=sQuery(id+"F0.wireOp",EDGE,"E91.bottom");var subQ317=sQuery(id+"F0.wireOp",EDGE,"E91.top");var subQ318=sQuery(id+"F0.wireOp",EDGE,"E91.left");var subQ319=sQuery(id+"F0.wireOp",EDGE,"E91.right");Q0=makeQuery(id+"F3.boolean.opBoolean","SPLIT",FACE,{"disambiguationData":[TD([makeQuery(id+"F1.opExtrude","SWEPT_FACE",FACE,{"disambiguationData":[OSD([subQ131])]})])],"derivedFrom":makeQuery(id+"F1.opExtrude","CAP_FACE",FACE,{"disambiguationData":[OSD([subQ131,subQ136,subQ137,subQ135,subQ128,subQ126,subQ125,subQ124,subQ123,subQ129,subQ138,subQ139,subQ140,subQ141,subQ142,subQ143,subQ144,subQ145,subQ146,subQ147,subQ148,subQ133,subQ122,subQ121,subQ120,subQ119,subQ118,subQ117,subQ116,subQ115,subQ114,subQ113,subQ112,subQ111,subQ110,subQ109,subQ108,subQ107,subQ106,subQ105,subQ104,subQ103,subQ102,subQ101,subQ100,subQ130,subQ149,subQ150,subQ151,subQ152,subQ153,subQ154,subQ155,subQ156,subQ157,subQ158,subQ159,subQ160,subQ161,subQ162,subQ163,subQ164,subQ165,subQ166,subQ167,subQ168,subQ169,subQ170,subQ171,subQ172,subQ173,subQ174,subQ175,subQ176,subQ177,subQ178,subQ179,subQ180,subQ181,subQ182,subQ183,subQ184,subQ185,subQ186,subQ187,subQ188,subQ189,subQ190,subQ191,subQ192,subQ193,subQ194,subQ195,subQ196,subQ197,subQ132,subQ99,subQ98,subQ97,subQ96,subQ95,subQ94,subQ93,subQ92,subQ91,subQ90,subQ89,subQ88,subQ87,subQ86,subQ85,subQ84,subQ83,subQ82,subQ81,subQ80,subQ79,subQ78,subQ77,subQ76,subQ75,subQ74,subQ73,subQ72,subQ71,subQ70,subQ69,subQ68,subQ67,subQ66,subQ65,subQ64,subQ63,subQ62,subQ61,subQ60,subQ59,subQ58,subQ57,subQ56,subQ55,subQ54,subQ53,subQ52,subQ51,subQ50,subQ49,subQ48,subQ47,subQ46,subQ45,subQ44,subQ43,subQ42,subQ41,subQ40,subQ39,subQ38,subQ37,subQ36,subQ35,subQ34,subQ33,subQ32,subQ31,subQ30,subQ29,subQ28,subQ27,subQ26,subQ25,subQ24,subQ23,subQ22,subQ21,subQ20,subQ19,subQ18,subQ17,subQ16,subQ15,subQ14,subQ13,subQ12,subQ11,subQ10,subQ9,subQ8,subQ7,subQ6,subQ5,subQ4,subQ3,subQ2,subQ1,subQ0,subQ134,subQ127,subQ198,subQ199,subQ200,subQ201,subQ202,subQ203,subQ204,subQ205,subQ206,subQ207,subQ208,subQ209,subQ210,subQ211,subQ212,subQ213,subQ214,subQ215,subQ216,subQ217,subQ218,subQ219,subQ220,subQ221,subQ222,subQ223,subQ224,subQ225,subQ226,subQ227,subQ228,subQ229,subQ230,subQ231,subQ232,subQ233,subQ234,subQ235,subQ236,subQ237,subQ238,subQ239,subQ240,subQ241,subQ242,subQ243,subQ244,subQ245,subQ246,subQ247,subQ248,subQ249,subQ250,subQ251,subQ252,subQ253,subQ254,subQ255,subQ256,subQ257,subQ258,subQ259,subQ260,subQ261,subQ262,subQ263,subQ264,subQ265,subQ266,subQ267,subQ268,subQ269,subQ270,subQ271,subQ272,subQ273,subQ274,subQ275,subQ276,subQ277,subQ278,subQ279,subQ280,subQ281,subQ282,subQ283,subQ284,subQ285,subQ286,subQ287,subQ288,subQ289,subQ290,subQ291,subQ292,subQ293,subQ294,subQ295,subQ296,subQ297,subQ298,subQ299,subQ300,subQ301,subQ302,subQ303,subQ304,subQ305,subQ306,subQ307,subQ308,subQ309,subQ310,subQ311,subQ312,subQ313,subQ314,subQ315,subQ316,subQ317,subQ318,subQ319])],"isStart":false})});}
            var sketch = newSketch(context, id + "F4", { "sketchPlane" : qUnion([Q0])});
            skText(sketch, "E93", { "text": "q-_-p", "fontName": "OpenSans-Bold.ttf"});
            const initialGuessF4  = {"E93": [0.1149, -0.00409, 1, 0, 0.00403]};
            skSetInitialGuess(sketch, initialGuessF4);
            skSolve(sketch);
        }
        {
            var Q0;
            Q0 = qSketchRegion(id + "F4", true);
            extrude(context, id + "F5", {"entities" : qUnion([Q0]), "operationType" : NewBodyOperationType.ADD, "depth" : 1 * mm, "offsetDistance" : 25 * mm});
        }
    });
